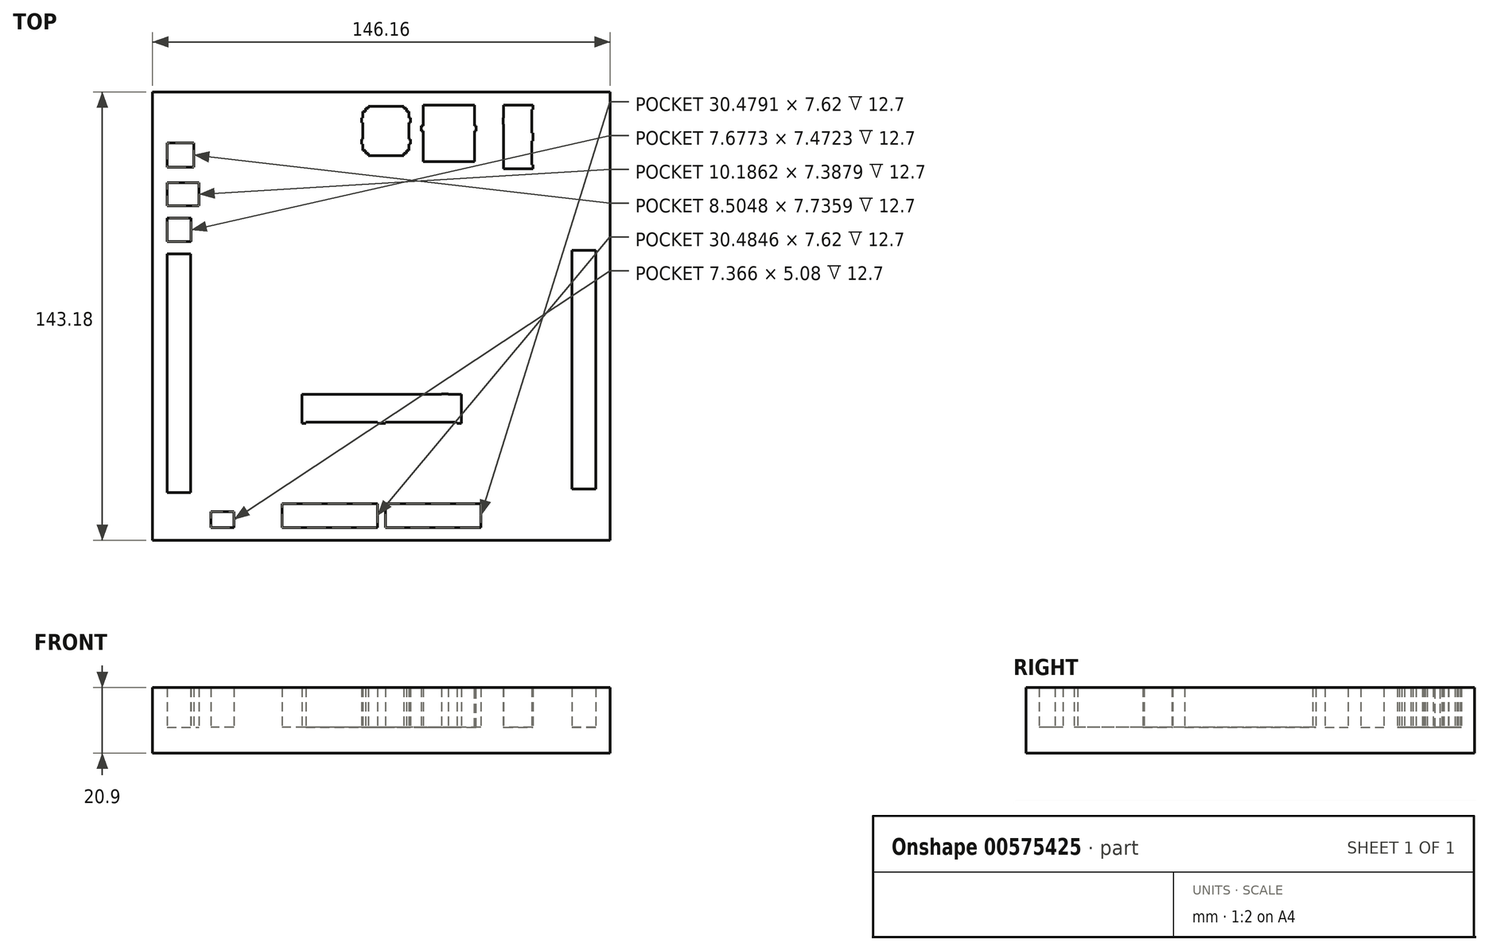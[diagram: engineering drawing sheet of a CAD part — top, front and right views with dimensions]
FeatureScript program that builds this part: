
annotation { "Feature Type Name" : "Feature", "Feature Type Description" : "" }
export const myFeature = defineFeature(function(context is Context, id is Id, definition is map)
    precondition{}
    {
        {
            var Q0;
            Q0=qCreatedBy(makeId("Top.planeOp"),FACE);
            var sketch = newSketch(context, id + "F0", { "sketchPlane" : qUnion([Q0])});
            skLineSegment(sketch, "E0.bottom", {"start": v(73.08, 71.59) * mm, "end": v(-73.08, 71.59) * mm});
            skLineSegment(sketch, "E0.top", {"start": v(73.08, -71.59) * mm, "end": v(-73.08, -71.59) * mm});
            skLineSegment(sketch, "E0.left", {"start": v(73.08, 71.59) * mm, "end": v(73.08, -71.59) * mm});
            skLineSegment(sketch, "E0.right", {"start": v(-73.08, 71.59) * mm, "end": v(-73.08, -71.59) * mm});
            skPoint(sketch, "E0.middle", {"position": v(0, 0) * mm});
            skSolve(sketch);
        }
        {
            var Q0;
            Q0=makeQuery(id+"F0.imprint","IMPRINT",FACE,{"disambiguationData":[TD([[makeQuery(id+"F0.imprint","IMPRINT",EDGE,{"derivedFrom":sQuery(id+"F0.wireOp",EDGE,"E0.bottom")}),1.0]])]});
            extrude(context, id + "F1", {"entities" : qUnion([Q0]), "depth" : 20.9 * mm, "offsetDistance" : 25.4 * mm});
        }
        {
            var Q0;
            Q0=makeQuery(id+"F1.opExtrude","CAP_FACE",FACE,{"disambiguationData":[OSD([sQuery(id+"F0.wireOp",EDGE,"E0.bottom"),sQuery(id+"F0.wireOp",EDGE,"E0.top"),sQuery(id+"F0.wireOp",EDGE,"E0.left"),sQuery(id+"F0.wireOp",EDGE,"E0.right")])],"isStart":false});
            var sketch = newSketch(context, id + "F2", { "sketchPlane" : qUnion([Q0])});
            skLineSegment(sketch, "E1.bottom", {"start": v(68.45, 67.44) * mm, "end": v(-68.45, 67.44) * mm});
            skLineSegment(sketch, "E1.top", {"start": v(68.45, -67.44) * mm, "end": v(-68.45, -67.44) * mm});
            skLineSegment(sketch, "E1.left", {"start": v(68.45, 67.44) * mm, "end": v(68.45, -67.44) * mm});
            skLineSegment(sketch, "E1.right", {"start": v(-68.45, 67.44) * mm, "end": v(-68.45, -67.44) * mm});
            skPoint(sketch, "E1.middle", {"position": v(0, 0) * mm});
            skSolve(sketch);
        }
        {
            var Q0;
            Q0=makeQuery(id+"F2.imprint","IMPRINT",FACE,{"disambiguationData":[TD([[makeQuery(id+"F2.imprint","IMPRINT",EDGE,{"derivedFrom":sQuery(id+"F2.wireOp",EDGE,"E1.bottom")}),1.0]])]});
            extrude(context, id + "F3", {"entities" : qUnion([Q0]), "operationType" : NewBodyOperationType.REMOVE, "oppositeDirection" : true, "depth" : 12.7 * mm, "offsetDistance" : 25.4 * mm});
        }
        {
            var Q0;
            Q0=makeQuery(id+"F3.boolean.opBoolean","COPY",FACE,{"derivedFrom":makeQuery(id+"F3.opExtrude","CAP_FACE",FACE,{"disambiguationData":[OSD([sQuery(id+"F2.wireOp",EDGE,"E1.bottom"),sQuery(id+"F2.wireOp",EDGE,"E1.top"),sQuery(id+"F2.wireOp",EDGE,"E1.left"),sQuery(id+"F2.wireOp",EDGE,"E1.right")])],"isStart":false})});
            var sketch = newSketch(context, id + "F4", { "sketchPlane" : qUnion([Q0])});
            skLineSegment(sketch, "E2.bottom", {"start": v(-68.45, -56.26) * mm, "end": v(-54.48, -56.26) * mm});
            skLineSegment(sketch, "E2.top", {"start": v(-68.45, -67.44) * mm, "end": v(-54.48, -67.44) * mm});
            skLineSegment(sketch, "E2.left", {"start": v(-68.45, -56.26) * mm, "end": v(-68.45, -67.44) * mm});
            skLineSegment(sketch, "E2.right", {"start": v(-54.48, -56.26) * mm, "end": v(-54.48, -67.44) * mm});
            skSolve(sketch);
        }
        {
            var Q0;
            Q0=makeQuery(id+"F4.imprint","IMPRINT",FACE,{"disambiguationData":[TD([[makeQuery(id+"F4.imprint","IMPRINT",EDGE,{"derivedFrom":sQuery(id+"F4.wireOp",EDGE,"E2.bottom")}),-1.0]])]});
            extrude(context, id + "F5", {"entities" : qUnion([Q0]), "operationType" : NewBodyOperationType.ADD, "depth" : 12.7 * mm, "offsetDistance" : 25.4 * mm});
        }
        {
            var Q0;
            Q0=makeQuery(id+"F3.boolean.opBoolean","COPY",FACE,{"derivedFrom":makeQuery(id+"F3.opExtrude","CAP_FACE",FACE,{"disambiguationData":[OSD([sQuery(id+"F2.wireOp",EDGE,"E1.bottom"),sQuery(id+"F2.wireOp",EDGE,"E1.top"),sQuery(id+"F2.wireOp",EDGE,"E1.left"),sQuery(id+"F2.wireOp",EDGE,"E1.right")])],"isStart":false})});
            var sketch = newSketch(context, id + "F6", { "sketchPlane" : qUnion([Q0])});
            skLineSegment(sketch, "E3.bottom", {"start": v(-54.48, -56.26) * mm, "end": v(-31.75, -56.26) * mm});
            skLineSegment(sketch, "E3.top", {"start": v(-54.48, -62.36) * mm, "end": v(-31.75, -62.36) * mm});
            skLineSegment(sketch, "E3.left", {"start": v(-54.48, -56.26) * mm, "end": v(-54.48, -62.36) * mm});
            skLineSegment(sketch, "E3.right", {"start": v(-31.75, -56.26) * mm, "end": v(-31.75, -62.36) * mm});
            skSolve(sketch);
        }
        {
            var Q0;
            Q0=makeQuery(id+"F6.imprint","IMPRINT",FACE,{"disambiguationData":[TD([[makeQuery(id+"F6.imprint","IMPRINT",EDGE,{"derivedFrom":sQuery(id+"F6.wireOp",EDGE,"E3.bottom")}),-1.0]])]});
            extrude(context, id + "F7", {"entities" : qUnion([Q0]), "operationType" : NewBodyOperationType.ADD, "depth" : 12.7 * mm, "offsetDistance" : 25.4 * mm});
        }
        {
            var Q0;
            Q0=makeQuery(id+"F3.boolean.opBoolean","COPY",FACE,{"derivedFrom":makeQuery(id+"F3.opExtrude","CAP_FACE",FACE,{"disambiguationData":[OSD([sQuery(id+"F2.wireOp",EDGE,"E1.bottom"),sQuery(id+"F2.wireOp",EDGE,"E1.top"),sQuery(id+"F2.wireOp",EDGE,"E1.left"),sQuery(id+"F2.wireOp",EDGE,"E1.right")])],"isStart":false})});
            var sketch = newSketch(context, id + "F8", { "sketchPlane" : qUnion([Q0])});
            skLineSegment(sketch, "E4.bottom", {"start": v(-31.75, -62.36) * mm, "end": v(-47.12, -62.36) * mm});
            skLineSegment(sketch, "E4.top", {"start": v(-31.75, -67.44) * mm, "end": v(-47.12, -67.44) * mm});
            skLineSegment(sketch, "E4.left", {"start": v(-31.75, -62.36) * mm, "end": v(-31.75, -67.44) * mm});
            skLineSegment(sketch, "E4.right", {"start": v(-47.12, -62.36) * mm, "end": v(-47.12, -67.44) * mm});
            skSolve(sketch);
        }
        {
            var Q0;
            Q0=makeQuery(id+"F8.imprint","IMPRINT",FACE,{"disambiguationData":[TD([[makeQuery(id+"F8.imprint","IMPRINT",EDGE,{"derivedFrom":sQuery(id+"F8.wireOp",EDGE,"E4.bottom")}),-1.0]])]});
            extrude(context, id + "F9", {"entities" : qUnion([Q0]), "operationType" : NewBodyOperationType.ADD, "depth" : 12.7 * mm, "offsetDistance" : 25.4 * mm});
        }
        {
            var Q0;
            {var subQ0=sQuery(id+"F2.wireOp",EDGE,"E1.right");var subQ1=sQuery(id+"F2.wireOp",EDGE,"E1.left");var subQ2=sQuery(id+"F2.wireOp",EDGE,"E1.top");var subQ3=sQuery(id+"F2.wireOp",EDGE,"E1.bottom");Q0=makeQuery(id+"F9.boolean.opBoolean","SPLIT",FACE,{"disambiguationData":[TD([makeQuery(id+"F3.boolean.opBoolean","COPY",FACE,{"derivedFrom":makeQuery(id+"F3.opExtrude","SWEPT_FACE",FACE,{"disambiguationData":[OSD([subQ3])]})})])],"derivedFrom":makeQuery(id+"F3.boolean.opBoolean","COPY",FACE,{"derivedFrom":makeQuery(id+"F3.opExtrude","CAP_FACE",FACE,{"disambiguationData":[OSD([subQ3,subQ2,subQ1,subQ0])],"isStart":false})})});}
            var sketch = newSketch(context, id + "F10", { "sketchPlane" : qUnion([Q0])});
            skLineSegment(sketch, "E5.bottom", {"start": v(68.45, -55.12) * mm, "end": v(31.75, -55.12) * mm});
            skLineSegment(sketch, "E5.top", {"start": v(68.45, -67.44) * mm, "end": v(31.75, -67.44) * mm});
            skLineSegment(sketch, "E5.left", {"start": v(68.45, -55.12) * mm, "end": v(68.45, -67.44) * mm});
            skLineSegment(sketch, "E5.right", {"start": v(31.75, -55.12) * mm, "end": v(31.75, -67.44) * mm});
            skSolve(sketch);
        }
        {
            var Q0;
            Q0=makeQuery(id+"F10.imprint","IMPRINT",FACE,{"disambiguationData":[TD([[makeQuery(id+"F10.imprint","IMPRINT",EDGE,{"derivedFrom":sQuery(id+"F10.wireOp",EDGE,"E5.bottom")}),1.0]])]});
            extrude(context, id + "F11", {"entities" : qUnion([Q0]), "operationType" : NewBodyOperationType.ADD, "depth" : 12.7 * mm, "offsetDistance" : 25.4 * mm});
        }
        {
            var Q0;
            {var subQ0=sQuery(id+"F2.wireOp",EDGE,"E1.right");var subQ1=sQuery(id+"F2.wireOp",EDGE,"E1.left");var subQ2=sQuery(id+"F2.wireOp",EDGE,"E1.top");var subQ3=sQuery(id+"F2.wireOp",EDGE,"E1.bottom");Q0=makeQuery(id+"F9.boolean.opBoolean","SPLIT",FACE,{"disambiguationData":[TD([makeQuery(id+"F3.boolean.opBoolean","COPY",FACE,{"derivedFrom":makeQuery(id+"F3.opExtrude","SWEPT_FACE",FACE,{"disambiguationData":[OSD([subQ3])]})})])],"derivedFrom":makeQuery(id+"F3.boolean.opBoolean","COPY",FACE,{"derivedFrom":makeQuery(id+"F3.opExtrude","CAP_FACE",FACE,{"disambiguationData":[OSD([subQ3,subQ2,subQ1,subQ0])],"isStart":false})})});}
            var sketch = newSketch(context, id + "F12", { "sketchPlane" : qUnion([Q0])});
            skLineSegment(sketch, "E6.bottom", {"start": v(31.75, -55.12) * mm, "end": v(-60.9, -55.12) * mm});
            skLineSegment(sketch, "E6.top", {"start": v(31.75, -59.82) * mm, "end": v(-60.9, -59.82) * mm});
            skLineSegment(sketch, "E6.left", {"start": v(31.75, -55.12) * mm, "end": v(31.75, -59.82) * mm});
            skLineSegment(sketch, "E6.right", {"start": v(-60.9, -55.12) * mm, "end": v(-60.9, -59.82) * mm});
            skLineSegment(sketch, "E7.left", {"start": v(31.75, -56.26) * mm, "end": v(31.75, -57.82) * mm});
            skSolve(sketch);
        }
        {
            var Q0;
            {var subQ9=sQuery(id+"F12.wireOp",EDGE,"E6.bottom");Q0=makeQuery(id+"F12.imprint","IMPRINT",FACE,{"disambiguationData":[TD([[makeQuery(id+"F12.imprint","IMPRINT",EDGE,{"derivedFrom":subQ9}),1.0]])]});}
            extrude(context, id + "F13", {"entities" : qUnion([Q0]), "operationType" : NewBodyOperationType.ADD, "depth" : 12.7 * mm, "offsetDistance" : 25.4 * mm});
        }
        {
            var Q0;
            {var subQ0=sQuery(id+"F2.wireOp",EDGE,"E1.right");var subQ3=sQuery(id+"F2.wireOp",EDGE,"E1.left");var subQ5=sQuery(id+"F2.wireOp",EDGE,"E1.bottom");var subQ6=makeQuery(id+"F3.boolean.opBoolean","COPY",FACE,{"derivedFrom":makeQuery(id+"F3.opExtrude","SWEPT_FACE",FACE,{"disambiguationData":[OSD([subQ5])]})});var subQ8=sQuery(id+"F2.wireOp",EDGE,"E1.top");Q0=makeQuery(id+"F13.boolean.opBoolean","SPLIT",FACE,{"disambiguationData":[TD([subQ6])],"derivedFrom":makeQuery(id+"F9.boolean.opBoolean","SPLIT",FACE,{"disambiguationData":[TD([subQ6])],"derivedFrom":makeQuery(id+"F3.boolean.opBoolean","COPY",FACE,{"derivedFrom":makeQuery(id+"F3.opExtrude","CAP_FACE",FACE,{"disambiguationData":[OSD([subQ5,subQ8,subQ3,subQ0])],"isStart":false})})})});}
            var sketch = newSketch(context, id + "F14", { "sketchPlane" : qUnion([Q0])});
            skLineSegment(sketch, "E8.bottom", {"start": v(-24.12, -33.89) * mm, "end": v(-1.28, -33.89) * mm});
            skLineSegment(sketch, "E8.top", {"start": v(-24.12, -55.12) * mm, "end": v(-1.28, -55.12) * mm});
            skLineSegment(sketch, "E8.left", {"start": v(-24.12, -33.89) * mm, "end": v(-24.12, -55.12) * mm});
            skLineSegment(sketch, "E8.right", {"start": v(-1.28, -33.89) * mm, "end": v(-1.28, -55.12) * mm});
            skSolve(sketch);
        }
        {
            var Q0;
            Q0=makeQuery(id+"F14.imprint","IMPRINT",FACE,{"disambiguationData":[TD([[makeQuery(id+"F14.imprint","IMPRINT",EDGE,{"derivedFrom":sQuery(id+"F14.wireOp",EDGE,"E8.bottom")}),-1.0]])]});
            extrude(context, id + "F15", {"entities" : qUnion([Q0]), "operationType" : NewBodyOperationType.ADD, "depth" : 12.7 * mm, "offsetDistance" : 25.4 * mm});
        }
        {
            var Q0;
            {var subQ0=sQuery(id+"F2.wireOp",EDGE,"E1.right");var subQ3=sQuery(id+"F2.wireOp",EDGE,"E1.left");var subQ5=sQuery(id+"F2.wireOp",EDGE,"E1.bottom");var subQ6=makeQuery(id+"F3.boolean.opBoolean","COPY",FACE,{"derivedFrom":makeQuery(id+"F3.opExtrude","SWEPT_FACE",FACE,{"disambiguationData":[OSD([subQ5])]})});var subQ8=sQuery(id+"F2.wireOp",EDGE,"E1.top");Q0=makeQuery(id+"F13.boolean.opBoolean","SPLIT",FACE,{"disambiguationData":[TD([subQ6])],"derivedFrom":makeQuery(id+"F9.boolean.opBoolean","SPLIT",FACE,{"disambiguationData":[TD([subQ6])],"derivedFrom":makeQuery(id+"F3.boolean.opBoolean","COPY",FACE,{"derivedFrom":makeQuery(id+"F3.opExtrude","CAP_FACE",FACE,{"disambiguationData":[OSD([subQ5,subQ8,subQ3,subQ0])],"isStart":false})})})});}
            var sketch = newSketch(context, id + "F16", { "sketchPlane" : qUnion([Q0])});
            skLineSegment(sketch, "E9.bottom", {"start": v(-1.28, -55.12) * mm, "end": v(1.76, -55.12) * mm});
            skLineSegment(sketch, "E9.top", {"start": v(-1.28, -34.27) * mm, "end": v(1.76, -34.27) * mm});
            skLineSegment(sketch, "E9.left", {"start": v(-1.28, -55.12) * mm, "end": v(-1.28, -34.27) * mm});
            skLineSegment(sketch, "E9.right", {"start": v(1.76, -55.12) * mm, "end": v(1.76, -34.27) * mm});
            skSolve(sketch);
        }
        {
            var Q0;
            Q0=makeQuery(id+"F16.imprint","IMPRINT",FACE,{"disambiguationData":[TD([[makeQuery(id+"F16.imprint","IMPRINT",EDGE,{"derivedFrom":sQuery(id+"F16.wireOp",EDGE,"E9.bottom")}),-1.0]])]});
            extrude(context, id + "F17", {"entities" : qUnion([Q0]), "operationType" : NewBodyOperationType.ADD, "depth" : 12.7 * mm, "offsetDistance" : 25.4 * mm});
        }
        {
            var Q0;
            {var subQ0=sQuery(id+"F2.wireOp",EDGE,"E1.right");var subQ3=sQuery(id+"F2.wireOp",EDGE,"E1.left");var subQ5=sQuery(id+"F2.wireOp",EDGE,"E1.bottom");var subQ6=makeQuery(id+"F3.boolean.opBoolean","COPY",FACE,{"derivedFrom":makeQuery(id+"F3.opExtrude","SWEPT_FACE",FACE,{"disambiguationData":[OSD([subQ5])]})});var subQ8=sQuery(id+"F2.wireOp",EDGE,"E1.top");Q0=makeQuery(id+"F13.boolean.opBoolean","SPLIT",FACE,{"disambiguationData":[TD([subQ6])],"derivedFrom":makeQuery(id+"F9.boolean.opBoolean","SPLIT",FACE,{"disambiguationData":[TD([subQ6])],"derivedFrom":makeQuery(id+"F3.boolean.opBoolean","COPY",FACE,{"derivedFrom":makeQuery(id+"F3.opExtrude","CAP_FACE",FACE,{"disambiguationData":[OSD([subQ5,subQ8,subQ3,subQ0])],"isStart":false})})})});}
            var sketch = newSketch(context, id + "F18", { "sketchPlane" : qUnion([Q0])});
            skLineSegment(sketch, "E10.bottom", {"start": v(1.26, -33.89) * mm, "end": v(24.12, -33.89) * mm});
            skLineSegment(sketch, "E10.top", {"start": v(1.26, -55.12) * mm, "end": v(24.12, -55.12) * mm});
            skLineSegment(sketch, "E10.left", {"start": v(1.26, -33.89) * mm, "end": v(1.26, -55.12) * mm});
            skLineSegment(sketch, "E10.right", {"start": v(24.12, -33.89) * mm, "end": v(24.12, -55.12) * mm});
            skSolve(sketch);
        }
        {
            var Q0;
            {var subQ1=sQuery(id+"F18.wireOp",EDGE,"E10.bottom");Q0=makeQuery(id+"F18.imprint","IMPRINT",FACE,{"disambiguationData":[TD([[makeQuery(id+"F18.imprint","IMPRINT",EDGE,{"derivedFrom":subQ1}),-1.0]])]});}
            extrude(context, id + "F19", {"entities" : qUnion([Q0]), "operationType" : NewBodyOperationType.ADD, "depth" : 12.7 * mm, "offsetDistance" : 25.4 * mm});
        }
        {
            var Q0;
            {var subQ0=sQuery(id+"F2.wireOp",EDGE,"E1.right");var subQ3=sQuery(id+"F2.wireOp",EDGE,"E1.left");var subQ5=sQuery(id+"F2.wireOp",EDGE,"E1.bottom");var subQ6=makeQuery(id+"F3.boolean.opBoolean","COPY",FACE,{"derivedFrom":makeQuery(id+"F3.opExtrude","SWEPT_FACE",FACE,{"disambiguationData":[OSD([subQ5])]})});var subQ8=sQuery(id+"F2.wireOp",EDGE,"E1.top");Q0=makeQuery(id+"F13.boolean.opBoolean","SPLIT",FACE,{"disambiguationData":[TD([subQ6])],"derivedFrom":makeQuery(id+"F9.boolean.opBoolean","SPLIT",FACE,{"disambiguationData":[TD([subQ6])],"derivedFrom":makeQuery(id+"F3.boolean.opBoolean","COPY",FACE,{"derivedFrom":makeQuery(id+"F3.opExtrude","CAP_FACE",FACE,{"disambiguationData":[OSD([subQ5,subQ8,subQ3,subQ0])],"isStart":false})})})});}
            var sketch = newSketch(context, id + "F20", { "sketchPlane" : qUnion([Q0])});
            skLineSegment(sketch, "E11.bottom", {"start": v(-24.14, -33.89) * mm, "end": v(-24.12, -33.89) * mm});
            skLineSegment(sketch, "E11.top", {"start": v(-24.14, -55.12) * mm, "end": v(-24.12, -55.12) * mm});
            skLineSegment(sketch, "E11.left", {"start": v(-24.14, -33.89) * mm, "end": v(-24.14, -55.12) * mm});
            skLineSegment(sketch, "E11.right", {"start": v(-24.12, -33.89) * mm, "end": v(-24.12, -55.12) * mm});
            skSolve(sketch);
        }
        {
            var Q0;
            Q0=makeQuery(id+"F20.imprint","IMPRINT",FACE,{"disambiguationData":[TD([[makeQuery(id+"F20.imprint","IMPRINT",EDGE,{"derivedFrom":sQuery(id+"F20.wireOp",EDGE,"E11.bottom")}),-1.0]])]});
            extrude(context, id + "F21", {"entities" : qUnion([Q0]), "operationType" : NewBodyOperationType.ADD, "depth" : 12.7 * mm, "offsetDistance" : 25.4 * mm});
        }
        {
            var Q0;
            {var subQ0=sQuery(id+"F2.wireOp",EDGE,"E1.right");var subQ3=sQuery(id+"F2.wireOp",EDGE,"E1.left");var subQ5=sQuery(id+"F2.wireOp",EDGE,"E1.bottom");var subQ6=makeQuery(id+"F3.boolean.opBoolean","COPY",FACE,{"derivedFrom":makeQuery(id+"F3.opExtrude","SWEPT_FACE",FACE,{"disambiguationData":[OSD([subQ5])]})});var subQ8=sQuery(id+"F2.wireOp",EDGE,"E1.top");Q0=makeQuery(id+"F13.boolean.opBoolean","SPLIT",FACE,{"disambiguationData":[TD([subQ6])],"derivedFrom":makeQuery(id+"F9.boolean.opBoolean","SPLIT",FACE,{"disambiguationData":[TD([subQ6])],"derivedFrom":makeQuery(id+"F3.boolean.opBoolean","COPY",FACE,{"derivedFrom":makeQuery(id+"F3.opExtrude","CAP_FACE",FACE,{"disambiguationData":[OSD([subQ5,subQ8,subQ3,subQ0])],"isStart":false})})})});}
            var sketch = newSketch(context, id + "F22", { "sketchPlane" : qUnion([Q0])});
            skLineSegment(sketch, "E12.bottom", {"start": v(24.12, -34.25) * mm, "end": v(60.83, -34.25) * mm});
            skLineSegment(sketch, "E12.top", {"start": v(24.12, -55.12) * mm, "end": v(60.83, -55.12) * mm});
            skLineSegment(sketch, "E12.left", {"start": v(24.12, -34.25) * mm, "end": v(24.12, -55.12) * mm});
            skLineSegment(sketch, "E12.right", {"start": v(60.83, -34.25) * mm, "end": v(60.83, -55.12) * mm});
            skSolve(sketch);
        }
        {
            var Q0;
            Q0=makeQuery(id+"F22.imprint","IMPRINT",FACE,{"disambiguationData":[TD([[makeQuery(id+"F22.imprint","IMPRINT",EDGE,{"derivedFrom":sQuery(id+"F22.wireOp",EDGE,"E12.bottom")}),-1.0]])]});
            extrude(context, id + "F23", {"entities" : qUnion([Q0]), "operationType" : NewBodyOperationType.ADD, "depth" : 12.7 * mm, "offsetDistance" : 25.4 * mm});
        }
        {
            var Q0;
            {var subQ0=sQuery(id+"F2.wireOp",EDGE,"E1.right");var subQ3=sQuery(id+"F2.wireOp",EDGE,"E1.left");var subQ5=sQuery(id+"F2.wireOp",EDGE,"E1.bottom");var subQ6=makeQuery(id+"F3.boolean.opBoolean","COPY",FACE,{"derivedFrom":makeQuery(id+"F3.opExtrude","SWEPT_FACE",FACE,{"disambiguationData":[OSD([subQ5])]})});var subQ8=sQuery(id+"F2.wireOp",EDGE,"E1.top");Q0=makeQuery(id+"F13.boolean.opBoolean","SPLIT",FACE,{"disambiguationData":[TD([subQ6])],"derivedFrom":makeQuery(id+"F9.boolean.opBoolean","SPLIT",FACE,{"disambiguationData":[TD([subQ6])],"derivedFrom":makeQuery(id+"F3.boolean.opBoolean","COPY",FACE,{"derivedFrom":makeQuery(id+"F3.opExtrude","CAP_FACE",FACE,{"disambiguationData":[OSD([subQ5,subQ8,subQ3,subQ0])],"isStart":false})})})});}
            var sketch = newSketch(context, id + "F24", { "sketchPlane" : qUnion([Q0])});
            skLineSegment(sketch, "E13.bottom", {"start": v(60.83, -20.99) * mm, "end": v(25.53, -20.99) * mm});
            skLineSegment(sketch, "E13.top", {"start": v(60.83, -34.25) * mm, "end": v(25.53, -34.25) * mm});
            skLineSegment(sketch, "E13.left", {"start": v(60.83, -20.99) * mm, "end": v(60.83, -34.25) * mm});
            skLineSegment(sketch, "E13.right", {"start": v(25.53, -20.99) * mm, "end": v(25.53, -34.25) * mm});
            skSolve(sketch);
        }
        {
            var Q0;
            Q0=makeQuery(id+"F24.imprint","IMPRINT",FACE,{"disambiguationData":[TD([[makeQuery(id+"F24.imprint","IMPRINT",EDGE,{"derivedFrom":sQuery(id+"F24.wireOp",EDGE,"E13.bottom")}),1.0]])]});
            extrude(context, id + "F25", {"entities" : qUnion([Q0]), "operationType" : NewBodyOperationType.ADD, "depth" : 12.7 * mm, "offsetDistance" : 25.4 * mm});
        }
        {
            var Q0;
            {var subQ0=sQuery(id+"F2.wireOp",EDGE,"E1.right");var subQ3=sQuery(id+"F2.wireOp",EDGE,"E1.left");var subQ5=sQuery(id+"F2.wireOp",EDGE,"E1.bottom");var subQ6=makeQuery(id+"F3.boolean.opBoolean","COPY",FACE,{"derivedFrom":makeQuery(id+"F3.opExtrude","SWEPT_FACE",FACE,{"disambiguationData":[OSD([subQ5])]})});var subQ8=sQuery(id+"F2.wireOp",EDGE,"E1.top");Q0=makeQuery(id+"F13.boolean.opBoolean","SPLIT",FACE,{"disambiguationData":[TD([subQ6])],"derivedFrom":makeQuery(id+"F9.boolean.opBoolean","SPLIT",FACE,{"disambiguationData":[TD([subQ6])],"derivedFrom":makeQuery(id+"F3.boolean.opBoolean","COPY",FACE,{"derivedFrom":makeQuery(id+"F3.opExtrude","CAP_FACE",FACE,{"disambiguationData":[OSD([subQ5,subQ8,subQ3,subQ0])],"isStart":false})})})});}
            var sketch = newSketch(context, id + "F26", { "sketchPlane" : qUnion([Q0])});
            skLineSegment(sketch, "E14.bottom", {"start": v(-60.92, -20.99) * mm, "end": v(-25.62, -20.99) * mm});
            skLineSegment(sketch, "E14.top", {"start": v(-60.92, -55.12) * mm, "end": v(-25.62, -55.12) * mm});
            skLineSegment(sketch, "E14.left", {"start": v(-60.92, -20.99) * mm, "end": v(-60.92, -55.12) * mm});
            skLineSegment(sketch, "E14.right", {"start": v(-25.62, -20.99) * mm, "end": v(-25.62, -55.12) * mm});
            skSolve(sketch);
        }
        {
            var Q0;
            Q0=makeQuery(id+"F26.imprint","IMPRINT",FACE,{"disambiguationData":[TD([[makeQuery(id+"F26.imprint","IMPRINT",EDGE,{"derivedFrom":sQuery(id+"F26.wireOp",EDGE,"E14.bottom")}),-1.0]])]});
            extrude(context, id + "F27", {"entities" : qUnion([Q0]), "operationType" : NewBodyOperationType.ADD, "depth" : 12.7 * mm, "offsetDistance" : 25.4 * mm});
        }
        {
            var Q0;
            {var subQ0=sQuery(id+"F2.wireOp",EDGE,"E1.right");var subQ3=sQuery(id+"F2.wireOp",EDGE,"E1.left");var subQ5=sQuery(id+"F2.wireOp",EDGE,"E1.bottom");var subQ6=makeQuery(id+"F3.boolean.opBoolean","COPY",FACE,{"derivedFrom":makeQuery(id+"F3.opExtrude","SWEPT_FACE",FACE,{"disambiguationData":[OSD([subQ5])]})});var subQ8=sQuery(id+"F2.wireOp",EDGE,"E1.top");Q0=makeQuery(id+"F13.boolean.opBoolean","SPLIT",FACE,{"disambiguationData":[TD([subQ6])],"derivedFrom":makeQuery(id+"F9.boolean.opBoolean","SPLIT",FACE,{"disambiguationData":[TD([subQ6])],"derivedFrom":makeQuery(id+"F3.boolean.opBoolean","COPY",FACE,{"derivedFrom":makeQuery(id+"F3.opExtrude","CAP_FACE",FACE,{"disambiguationData":[OSD([subQ5,subQ8,subQ3,subQ0])],"isStart":false})})})});}
            var sketch = newSketch(context, id + "F28", { "sketchPlane" : qUnion([Q0])});
            skPoint(sketch, "E15.firstSnap0", {"position": v(-0.01, -34.27) * mm});
            skLineSegment(sketch, "E15.bottom", {"start": v(-24.14, -34.27) * mm, "end": v(-25.62, -34.27) * mm});
            skLineSegment(sketch, "E15.top", {"start": v(-24.14, -55.12) * mm, "end": v(-25.62, -55.12) * mm});
            skLineSegment(sketch, "E15.left", {"start": v(-24.14, -34.27) * mm, "end": v(-24.14, -55.12) * mm});
            skLineSegment(sketch, "E15.right", {"start": v(-25.62, -34.27) * mm, "end": v(-25.62, -55.12) * mm});
            skSolve(sketch);
        }
        {
            var Q0;
            Q0=makeQuery(id+"F28.imprint","IMPRINT",FACE,{"disambiguationData":[TD([[makeQuery(id+"F28.imprint","IMPRINT",EDGE,{"derivedFrom":sQuery(id+"F28.wireOp",EDGE,"E15.bottom")}),1.0]])]});
            extrude(context, id + "F29", {"entities" : qUnion([Q0]), "operationType" : NewBodyOperationType.ADD, "depth" : 12.7 * mm, "offsetDistance" : 25.4 * mm});
        }
        {
            var Q0;
            {var subQ0=sQuery(id+"F2.wireOp",EDGE,"E1.right");var subQ3=sQuery(id+"F2.wireOp",EDGE,"E1.left");var subQ5=sQuery(id+"F2.wireOp",EDGE,"E1.bottom");var subQ6=makeQuery(id+"F3.boolean.opBoolean","COPY",FACE,{"derivedFrom":makeQuery(id+"F3.opExtrude","SWEPT_FACE",FACE,{"disambiguationData":[OSD([subQ5])]})});var subQ8=sQuery(id+"F2.wireOp",EDGE,"E1.top");Q0=makeQuery(id+"F13.boolean.opBoolean","SPLIT",FACE,{"disambiguationData":[TD([subQ6])],"derivedFrom":makeQuery(id+"F9.boolean.opBoolean","SPLIT",FACE,{"disambiguationData":[TD([subQ6])],"derivedFrom":makeQuery(id+"F3.boolean.opBoolean","COPY",FACE,{"derivedFrom":makeQuery(id+"F3.opExtrude","CAP_FACE",FACE,{"disambiguationData":[OSD([subQ5,subQ8,subQ3,subQ0])],"isStart":false})})})});}
            var sketch = newSketch(context, id + "F30", { "sketchPlane" : qUnion([Q0])});
            skLineSegment(sketch, "E16.bottom", {"start": v(-25.41, -34.27) * mm, "end": v(-25.62, -34.27) * mm});
            skLineSegment(sketch, "E16.top", {"start": v(-25.41, -20.99) * mm, "end": v(-25.62, -20.99) * mm});
            skLineSegment(sketch, "E16.left", {"start": v(-25.41, -34.27) * mm, "end": v(-25.41, -20.99) * mm});
            skLineSegment(sketch, "E16.right", {"start": v(-25.62, -34.27) * mm, "end": v(-25.62, -20.99) * mm});
            skSolve(sketch);
        }
        {
            var Q0;
            Q0=makeQuery(id+"F30.imprint","IMPRINT",FACE,{"disambiguationData":[TD([[makeQuery(id+"F30.imprint","IMPRINT",EDGE,{"derivedFrom":sQuery(id+"F30.wireOp",EDGE,"E16.bottom")}),-1.0]])]});
            extrude(context, id + "F31", {"entities" : qUnion([Q0]), "operationType" : NewBodyOperationType.ADD, "depth" : 12.7 * mm, "offsetDistance" : 25.4 * mm});
        }
        {
            var Q0;
            {var subQ0=sQuery(id+"F2.wireOp",EDGE,"E1.right");var subQ3=sQuery(id+"F2.wireOp",EDGE,"E1.left");var subQ5=sQuery(id+"F2.wireOp",EDGE,"E1.bottom");var subQ6=makeQuery(id+"F3.boolean.opBoolean","COPY",FACE,{"derivedFrom":makeQuery(id+"F3.opExtrude","SWEPT_FACE",FACE,{"disambiguationData":[OSD([subQ5])]})});var subQ8=sQuery(id+"F2.wireOp",EDGE,"E1.top");Q0=makeQuery(id+"F13.boolean.opBoolean","SPLIT",FACE,{"disambiguationData":[TD([subQ6])],"derivedFrom":makeQuery(id+"F9.boolean.opBoolean","SPLIT",FACE,{"disambiguationData":[TD([subQ6])],"derivedFrom":makeQuery(id+"F3.boolean.opBoolean","COPY",FACE,{"derivedFrom":makeQuery(id+"F3.opExtrude","CAP_FACE",FACE,{"disambiguationData":[OSD([subQ5,subQ8,subQ3,subQ0])],"isStart":false})})})});}
            var sketch = newSketch(context, id + "F32", { "sketchPlane" : qUnion([Q0])});
            skLineSegment(sketch, "E17.bottom", {"start": v(-25.41, -20.99) * mm, "end": v(25.53, -20.99) * mm});
            skLineSegment(sketch, "E17.top", {"start": v(-25.41, -24.8) * mm, "end": v(25.53, -24.8) * mm});
            skLineSegment(sketch, "E17.left", {"start": v(-25.41, -20.99) * mm, "end": v(-25.41, -24.8) * mm});
            skLineSegment(sketch, "E17.right", {"start": v(25.53, -20.99) * mm, "end": v(25.53, -24.8) * mm});
            skSolve(sketch);
        }
        {
            var Q0;
            Q0=makeQuery(id+"F32.imprint","IMPRINT",FACE,{"disambiguationData":[TD([[makeQuery(id+"F32.imprint","IMPRINT",EDGE,{"derivedFrom":sQuery(id+"F32.wireOp",EDGE,"E17.bottom")}),-1.0]])]});
            extrude(context, id + "F33", {"entities" : qUnion([Q0]), "operationType" : NewBodyOperationType.ADD, "depth" : 12.7 * mm, "offsetDistance" : 25.4 * mm});
        }
        {
            var Q0;
            {var subQ0=sQuery(id+"F2.wireOp",EDGE,"E1.right");var subQ3=sQuery(id+"F2.wireOp",EDGE,"E1.left");var subQ5=sQuery(id+"F2.wireOp",EDGE,"E1.bottom");var subQ6=makeQuery(id+"F3.boolean.opBoolean","COPY",FACE,{"derivedFrom":makeQuery(id+"F3.opExtrude","SWEPT_FACE",FACE,{"disambiguationData":[OSD([subQ5])]})});var subQ8=sQuery(id+"F2.wireOp",EDGE,"E1.top");Q0=makeQuery(id+"F33.boolean.opBoolean","SPLIT",FACE,{"disambiguationData":[TD([makeQuery(id+"F15.opExtrude","SWEPT_FACE",FACE,{"disambiguationData":[OSD([sQuery(id+"F14.wireOp",EDGE,"E8.bottom")])]})])],"derivedFrom":makeQuery(id+"F13.boolean.opBoolean","SPLIT",FACE,{"disambiguationData":[TD([subQ6])],"derivedFrom":makeQuery(id+"F9.boolean.opBoolean","SPLIT",FACE,{"disambiguationData":[TD([subQ6])],"derivedFrom":makeQuery(id+"F3.boolean.opBoolean","COPY",FACE,{"derivedFrom":makeQuery(id+"F3.opExtrude","CAP_FACE",FACE,{"disambiguationData":[OSD([subQ5,subQ8,subQ3,subQ0])],"isStart":false})})})})});}
            var sketch = newSketch(context, id + "F34", { "sketchPlane" : qUnion([Q0])});
            skLineSegment(sketch, "E18.bottom", {"start": v(25.53, -24.8) * mm, "end": v(21.33, -24.8) * mm});
            skLineSegment(sketch, "E18.top", {"start": v(25.53, -25) * mm, "end": v(21.33, -25) * mm});
            skLineSegment(sketch, "E18.left", {"start": v(25.53, -24.8) * mm, "end": v(25.53, -25) * mm});
            skLineSegment(sketch, "E18.right", {"start": v(21.33, -24.8) * mm, "end": v(21.33, -25) * mm});
            skLineSegment(sketch, "E19.bottom", {"start": v(25.53, -25) * mm, "end": v(25.39, -25) * mm});
            skLineSegment(sketch, "E19.top", {"start": v(25.53, -34.25) * mm, "end": v(25.39, -34.25) * mm});
            skLineSegment(sketch, "E19.left", {"start": v(25.53, -25) * mm, "end": v(25.53, -34.25) * mm});
            skLineSegment(sketch, "E19.right", {"start": v(25.39, -25) * mm, "end": v(25.39, -34.25) * mm});
            skSolve(sketch);
        }
        {
            var Q0;
            Q0=makeQuery(id+"F34.imprint","IMPRINT",FACE,{"disambiguationData":[TD([[makeQuery(id+"F34.imprint","IMPRINT",EDGE,{"derivedFrom":sQuery(id+"F34.wireOp",EDGE,"E19.bottom")}),1.0]])]});
            var Q1;
            Q1=makeQuery(id+"F34.imprint","IMPRINT",FACE,{"disambiguationData":[TD([[makeQuery(id+"F34.imprint","IMPRINT",EDGE,{"derivedFrom":sQuery(id+"F34.wireOp",EDGE,"E18.bottom")}),-1.0]])]});
            extrude(context, id + "F35", {"entities" : qUnion([Q0, Q1]), "operationType" : NewBodyOperationType.ADD, "depth" : 12.7 * mm, "offsetDistance" : 25.4 * mm});
        }
        {
            var Q0;
            {var subQ0=sQuery(id+"F2.wireOp",EDGE,"E1.right");var subQ3=sQuery(id+"F2.wireOp",EDGE,"E1.left");var subQ5=sQuery(id+"F2.wireOp",EDGE,"E1.bottom");var subQ6=makeQuery(id+"F3.boolean.opBoolean","COPY",FACE,{"derivedFrom":makeQuery(id+"F3.opExtrude","SWEPT_FACE",FACE,{"disambiguationData":[OSD([subQ5])]})});var subQ8=sQuery(id+"F2.wireOp",EDGE,"E1.top");Q0=makeQuery(id+"F33.boolean.opBoolean","SPLIT",FACE,{"disambiguationData":[TD([makeQuery(id+"F15.opExtrude","SWEPT_FACE",FACE,{"disambiguationData":[OSD([sQuery(id+"F14.wireOp",EDGE,"E8.bottom")])]})])],"derivedFrom":makeQuery(id+"F13.boolean.opBoolean","SPLIT",FACE,{"disambiguationData":[TD([subQ6])],"derivedFrom":makeQuery(id+"F9.boolean.opBoolean","SPLIT",FACE,{"disambiguationData":[TD([subQ6])],"derivedFrom":makeQuery(id+"F3.boolean.opBoolean","COPY",FACE,{"derivedFrom":makeQuery(id+"F3.opExtrude","CAP_FACE",FACE,{"disambiguationData":[OSD([subQ5,subQ8,subQ3,subQ0])],"isStart":false})})})})});}
            var sketch = newSketch(context, id + "F36", { "sketchPlane" : qUnion([Q0])});
            skLineSegment(sketch, "E20.bottom", {"start": v(19.3, -25) * mm, "end": v(-25.41, -25) * mm});
            skLineSegment(sketch, "E20.top", {"start": v(19.3, -24.8) * mm, "end": v(-25.41, -24.8) * mm});
            skLineSegment(sketch, "E20.left", {"start": v(19.3, -25) * mm, "end": v(19.3, -24.8) * mm});
            skLineSegment(sketch, "E20.right", {"start": v(-25.41, -25) * mm, "end": v(-25.41, -24.8) * mm});
            skSolve(sketch);
        }
        {
            var Q0;
            Q0=makeQuery(id+"F36.imprint","IMPRINT",FACE,{"disambiguationData":[TD([[makeQuery(id+"F36.imprint","IMPRINT",EDGE,{"derivedFrom":sQuery(id+"F36.wireOp",EDGE,"E20.bottom")}),-1.0]])]});
            extrude(context, id + "F37", {"entities" : qUnion([Q0]), "operationType" : NewBodyOperationType.ADD, "depth" : 12.7 * mm, "offsetDistance" : 25.4 * mm});
        }
        {
            var Q0;
            {var subQ3=sQuery(id+"F2.wireOp",EDGE,"E1.bottom");var subQ4=makeQuery(id+"F3.boolean.opBoolean","COPY",FACE,{"derivedFrom":makeQuery(id+"F3.opExtrude","SWEPT_FACE",FACE,{"disambiguationData":[OSD([subQ3])]})});var subQ5=sQuery(id+"F2.wireOp",EDGE,"E1.left");var subQ8=sQuery(id+"F2.wireOp",EDGE,"E1.right");var subQ11=sQuery(id+"F2.wireOp",EDGE,"E1.top");Q0=makeQuery(id+"F33.boolean.opBoolean","SPLIT",FACE,{"disambiguationData":[TD([subQ4])],"derivedFrom":makeQuery(id+"F13.boolean.opBoolean","SPLIT",FACE,{"disambiguationData":[TD([subQ4])],"derivedFrom":makeQuery(id+"F9.boolean.opBoolean","SPLIT",FACE,{"disambiguationData":[TD([subQ4])],"derivedFrom":makeQuery(id+"F3.boolean.opBoolean","COPY",FACE,{"derivedFrom":makeQuery(id+"F3.opExtrude","CAP_FACE",FACE,{"disambiguationData":[OSD([subQ3,subQ11,subQ5,subQ8])],"isStart":false})})})})});}
            var sketch = newSketch(context, id + "F38", { "sketchPlane" : qUnion([Q0])});
            skLineSegment(sketch, "E21.bottom", {"start": v(-68.45, 23.82) * mm, "end": v(-59.52, 23.82) * mm});
            skLineSegment(sketch, "E21.top", {"start": v(-68.45, 19.9) * mm, "end": v(-59.52, 19.9) * mm});
            skLineSegment(sketch, "E21.left", {"start": v(-68.45, 23.82) * mm, "end": v(-68.45, 19.9) * mm});
            skLineSegment(sketch, "E21.right", {"start": v(-59.52, 23.82) * mm, "end": v(-59.52, 19.9) * mm});
            skSolve(sketch);
        }
        {
            var Q0;
            Q0=makeQuery(id+"F38.imprint","IMPRINT",FACE,{"disambiguationData":[TD([[makeQuery(id+"F38.imprint","IMPRINT",EDGE,{"derivedFrom":sQuery(id+"F38.wireOp",EDGE,"E21.bottom")}),-1.0]])]});
            extrude(context, id + "F39", {"entities" : qUnion([Q0]), "operationType" : NewBodyOperationType.ADD, "depth" : 12.7 * mm, "offsetDistance" : 25.4 * mm});
        }
        {
            var Q0;
            {var subQ3=sQuery(id+"F2.wireOp",EDGE,"E1.bottom");var subQ4=makeQuery(id+"F3.boolean.opBoolean","COPY",FACE,{"derivedFrom":makeQuery(id+"F3.opExtrude","SWEPT_FACE",FACE,{"disambiguationData":[OSD([subQ3])]})});var subQ5=sQuery(id+"F2.wireOp",EDGE,"E1.left");var subQ8=sQuery(id+"F2.wireOp",EDGE,"E1.right");var subQ11=sQuery(id+"F2.wireOp",EDGE,"E1.top");Q0=makeQuery(id+"F33.boolean.opBoolean","SPLIT",FACE,{"disambiguationData":[TD([subQ4])],"derivedFrom":makeQuery(id+"F13.boolean.opBoolean","SPLIT",FACE,{"disambiguationData":[TD([subQ4])],"derivedFrom":makeQuery(id+"F9.boolean.opBoolean","SPLIT",FACE,{"disambiguationData":[TD([subQ4])],"derivedFrom":makeQuery(id+"F3.boolean.opBoolean","COPY",FACE,{"derivedFrom":makeQuery(id+"F3.opExtrude","CAP_FACE",FACE,{"disambiguationData":[OSD([subQ3,subQ11,subQ5,subQ8])],"isStart":false})})})})});}
            var sketch = newSketch(context, id + "F40", { "sketchPlane" : qUnion([Q0])});
            skLineSegment(sketch, "E22.bottom", {"start": v(-59.52, 23.82) * mm, "end": v(68.45, 23.82) * mm});
            skLineSegment(sketch, "E22.top", {"start": v(-59.52, 21.01) * mm, "end": v(68.45, 21.01) * mm});
            skLineSegment(sketch, "E22.left", {"start": v(-59.52, 23.82) * mm, "end": v(-59.52, 21.01) * mm});
            skLineSegment(sketch, "E22.right", {"start": v(68.45, 23.82) * mm, "end": v(68.45, 21.01) * mm});
            skSolve(sketch);
        }
        {
            var Q0;
            Q0=makeQuery(id+"F40.imprint","IMPRINT",FACE,{"disambiguationData":[TD([[makeQuery(id+"F40.imprint","IMPRINT",EDGE,{"derivedFrom":sQuery(id+"F40.wireOp",EDGE,"E22.bottom")}),-1.0]])]});
            extrude(context, id + "F41", {"entities" : qUnion([Q0]), "operationType" : NewBodyOperationType.ADD, "depth" : 12.7 * mm, "offsetDistance" : 25.4 * mm});
        }
        {
            var Q0;
            {var subQ5=sQuery(id+"F2.wireOp",EDGE,"E1.left");var subQ7=makeQuery(id+"F5.opExtrude","SWEPT_FACE",FACE,{"disambiguationData":[OSD([sQuery(id+"F4.wireOp",EDGE,"E2.bottom")])]});var subQ8=sQuery(id+"F2.wireOp",EDGE,"E1.right");var subQ17=sQuery(id+"F2.wireOp",EDGE,"E1.bottom");var subQ18=makeQuery(id+"F3.boolean.opBoolean","COPY",FACE,{"derivedFrom":makeQuery(id+"F3.opExtrude","SWEPT_FACE",FACE,{"disambiguationData":[OSD([subQ17])]})});var subQ19=sQuery(id+"F2.wireOp",EDGE,"E1.top");Q0=makeQuery(id+"F41.boolean.opBoolean","SPLIT",FACE,{"disambiguationData":[TD([subQ7])],"derivedFrom":makeQuery(id+"F33.boolean.opBoolean","SPLIT",FACE,{"disambiguationData":[TD([subQ18])],"derivedFrom":makeQuery(id+"F13.boolean.opBoolean","SPLIT",FACE,{"disambiguationData":[TD([subQ18])],"derivedFrom":makeQuery(id+"F9.boolean.opBoolean","SPLIT",FACE,{"disambiguationData":[TD([subQ18])],"derivedFrom":makeQuery(id+"F3.boolean.opBoolean","COPY",FACE,{"derivedFrom":makeQuery(id+"F3.opExtrude","CAP_FACE",FACE,{"disambiguationData":[OSD([subQ17,subQ19,subQ5,subQ8])],"isStart":false})})})})})});}
            var sketch = newSketch(context, id + "F42", { "sketchPlane" : qUnion([Q0])});
            skLineSegment(sketch, "E23.bottom", {"start": v(-59.52, 19.9) * mm, "end": v(60.87, 19.9) * mm});
            skLineSegment(sketch, "E23.top", {"start": v(-59.52, 21.01) * mm, "end": v(60.87, 21.01) * mm});
            skLineSegment(sketch, "E23.left", {"start": v(-59.52, 19.9) * mm, "end": v(-59.52, 21.01) * mm});
            skLineSegment(sketch, "E23.right", {"start": v(60.87, 19.9) * mm, "end": v(60.87, 21.01) * mm});
            skSolve(sketch);
        }
        {
            var Q0;
            Q0=makeQuery(id+"F42.imprint","IMPRINT",FACE,{"disambiguationData":[TD([[makeQuery(id+"F42.imprint","IMPRINT",EDGE,{"derivedFrom":sQuery(id+"F42.wireOp",EDGE,"E23.bottom")}),1.0]])]});
            extrude(context, id + "F43", {"entities" : qUnion([Q0]), "operationType" : NewBodyOperationType.ADD, "depth" : 12.7 * mm, "offsetDistance" : 25.4 * mm});
        }
        {
            var Q0;
            {var subQ5=sQuery(id+"F2.wireOp",EDGE,"E1.left");var subQ7=makeQuery(id+"F5.opExtrude","SWEPT_FACE",FACE,{"disambiguationData":[OSD([sQuery(id+"F4.wireOp",EDGE,"E2.bottom")])]});var subQ8=sQuery(id+"F2.wireOp",EDGE,"E1.right");var subQ17=sQuery(id+"F2.wireOp",EDGE,"E1.bottom");var subQ18=makeQuery(id+"F3.boolean.opBoolean","COPY",FACE,{"derivedFrom":makeQuery(id+"F3.opExtrude","SWEPT_FACE",FACE,{"disambiguationData":[OSD([subQ17])]})});var subQ19=sQuery(id+"F2.wireOp",EDGE,"E1.top");Q0=makeQuery(id+"F41.boolean.opBoolean","SPLIT",FACE,{"disambiguationData":[TD([subQ7])],"derivedFrom":makeQuery(id+"F33.boolean.opBoolean","SPLIT",FACE,{"disambiguationData":[TD([subQ18])],"derivedFrom":makeQuery(id+"F13.boolean.opBoolean","SPLIT",FACE,{"disambiguationData":[TD([subQ18])],"derivedFrom":makeQuery(id+"F9.boolean.opBoolean","SPLIT",FACE,{"disambiguationData":[TD([subQ18])],"derivedFrom":makeQuery(id+"F3.boolean.opBoolean","COPY",FACE,{"derivedFrom":makeQuery(id+"F3.opExtrude","CAP_FACE",FACE,{"disambiguationData":[OSD([subQ17,subQ19,subQ5,subQ8])],"isStart":false})})})})})});}
            var sketch = newSketch(context, id + "F44", { "sketchPlane" : qUnion([Q0])});
            skLineSegment(sketch, "E24.bottom", {"start": v(-60.92, -20.99) * mm, "end": v(60.87, -20.99) * mm});
            skLineSegment(sketch, "E24.top", {"start": v(-60.92, 19.9) * mm, "end": v(60.87, 19.9) * mm});
            skLineSegment(sketch, "E24.left", {"start": v(-60.92, -20.99) * mm, "end": v(-60.92, 19.9) * mm});
            skLineSegment(sketch, "E24.right", {"start": v(60.87, -20.99) * mm, "end": v(60.87, 19.9) * mm});
            skSolve(sketch);
        }
        {
            var Q0;
            Q0=makeQuery(id+"F44.imprint","IMPRINT",FACE,{"disambiguationData":[TD([[makeQuery(id+"F44.imprint","IMPRINT",EDGE,{"derivedFrom":sQuery(id+"F44.wireOp",EDGE,"E24.top")}),-1.0]])]});
            extrude(context, id + "F45", {"entities" : qUnion([Q0]), "operationType" : NewBodyOperationType.ADD, "depth" : 12.7 * mm, "offsetDistance" : 25.4 * mm});
        }
        {
            var Q0;
            {var subQ0=sQuery(id+"F2.wireOp",EDGE,"E1.right");var subQ2=sQuery(id+"F2.wireOp",EDGE,"E1.left");var subQ4=sQuery(id+"F2.wireOp",EDGE,"E1.bottom");var subQ5=makeQuery(id+"F3.boolean.opBoolean","COPY",FACE,{"derivedFrom":makeQuery(id+"F3.opExtrude","SWEPT_FACE",FACE,{"disambiguationData":[OSD([subQ4])]})});var subQ11=sQuery(id+"F2.wireOp",EDGE,"E1.top");Q0=makeQuery(id+"F41.boolean.opBoolean","SPLIT",FACE,{"disambiguationData":[TD([subQ5])],"derivedFrom":makeQuery(id+"F33.boolean.opBoolean","SPLIT",FACE,{"disambiguationData":[TD([subQ5])],"derivedFrom":makeQuery(id+"F13.boolean.opBoolean","SPLIT",FACE,{"disambiguationData":[TD([subQ5])],"derivedFrom":makeQuery(id+"F9.boolean.opBoolean","SPLIT",FACE,{"disambiguationData":[TD([subQ5])],"derivedFrom":makeQuery(id+"F3.boolean.opBoolean","COPY",FACE,{"derivedFrom":makeQuery(id+"F3.opExtrude","CAP_FACE",FACE,{"disambiguationData":[OSD([subQ4,subQ11,subQ2,subQ0])],"isStart":false})})})})})});}
            var sketch = newSketch(context, id + "F46", { "sketchPlane" : qUnion([Q0])});
            skLineSegment(sketch, "E25.bottom", {"start": v(-68.45, 35.25) * mm, "end": v(-56.12, 35.25) * mm});
            skLineSegment(sketch, "E25.top", {"start": v(-68.45, 31.29) * mm, "end": v(-56.12, 31.29) * mm});
            skLineSegment(sketch, "E25.left", {"start": v(-68.45, 35.25) * mm, "end": v(-68.45, 31.29) * mm});
            skLineSegment(sketch, "E25.right", {"start": v(-56.12, 35.25) * mm, "end": v(-56.12, 31.29) * mm});
            skSolve(sketch);
        }
        {
            var Q0;
            Q0=makeQuery(id+"F46.imprint","IMPRINT",FACE,{"disambiguationData":[TD([[makeQuery(id+"F46.imprint","IMPRINT",EDGE,{"derivedFrom":sQuery(id+"F46.wireOp",EDGE,"E25.bottom")}),-1.0]])]});
            extrude(context, id + "F47", {"entities" : qUnion([Q0]), "operationType" : NewBodyOperationType.ADD, "depth" : 12.7 * mm, "offsetDistance" : 25.4 * mm});
        }
        {
            var Q0;
            {var subQ0=sQuery(id+"F2.wireOp",EDGE,"E1.right");var subQ2=sQuery(id+"F2.wireOp",EDGE,"E1.left");var subQ4=sQuery(id+"F2.wireOp",EDGE,"E1.bottom");var subQ5=makeQuery(id+"F3.boolean.opBoolean","COPY",FACE,{"derivedFrom":makeQuery(id+"F3.opExtrude","SWEPT_FACE",FACE,{"disambiguationData":[OSD([subQ4])]})});var subQ11=sQuery(id+"F2.wireOp",EDGE,"E1.top");Q0=makeQuery(id+"F41.boolean.opBoolean","SPLIT",FACE,{"disambiguationData":[TD([subQ5])],"derivedFrom":makeQuery(id+"F33.boolean.opBoolean","SPLIT",FACE,{"disambiguationData":[TD([subQ5])],"derivedFrom":makeQuery(id+"F13.boolean.opBoolean","SPLIT",FACE,{"disambiguationData":[TD([subQ5])],"derivedFrom":makeQuery(id+"F9.boolean.opBoolean","SPLIT",FACE,{"disambiguationData":[TD([subQ5])],"derivedFrom":makeQuery(id+"F3.boolean.opBoolean","COPY",FACE,{"derivedFrom":makeQuery(id+"F3.opExtrude","CAP_FACE",FACE,{"disambiguationData":[OSD([subQ4,subQ11,subQ2,subQ0])],"isStart":false})})})})})});}
            var sketch = newSketch(context, id + "F48", { "sketchPlane" : qUnion([Q0])});
            skLineSegment(sketch, "E26", {"start": v(-58.27, 35.25) * mm, "end": v(-58.27, 42.64) * mm});
            skLineSegment(sketch, "E27", {"start": v(-58.27, 42.64) * mm, "end": v(-68.45, 42.64) * mm});
            skLineSegment(sketch, "E28", {"start": v(-68.45, 42.64) * mm, "end": v(-68.45, 47.59) * mm});
            skLineSegment(sketch, "E29", {"start": v(-68.45, 47.59) * mm, "end": v(-56.12, 47.59) * mm});
            skLineSegment(sketch, "E30", {"start": v(-56.12, 47.59) * mm, "end": v(-56.12, 35.25) * mm});
            skLineSegment(sketch, "E31", {"start": v(-56.12, 35.25) * mm, "end": v(-58.27, 35.25) * mm});
            skLineSegment(sketch, "E32", {"start": v(-56.12, 31.29) * mm, "end": v(-56.12, 23.82) * mm});
            skLineSegment(sketch, "E33", {"start": v(-56.12, 23.82) * mm, "end": v(-60.78, 23.82) * mm});
            skLineSegment(sketch, "E34", {"start": v(-60.78, 23.82) * mm, "end": v(-60.78, 31.29) * mm});
            skLineSegment(sketch, "E35", {"start": v(-60.78, 31.29) * mm, "end": v(-56.12, 31.29) * mm});
            skLineSegment(sketch, "E36", {"start": v(-59.95, 47.59) * mm, "end": v(-59.95, 55.32) * mm});
            skLineSegment(sketch, "E37", {"start": v(-59.95, 55.32) * mm, "end": v(-68.45, 55.32) * mm});
            skLineSegment(sketch, "E38", {"start": v(-68.45, 55.32) * mm, "end": v(-68.45, 67.44) * mm});
            skLineSegment(sketch, "E39", {"start": v(-68.45, 67.44) * mm, "end": v(-7.62, 67.44) * mm});
            skLineSegment(sketch, "E40", {"start": v(-7.62, 67.44) * mm, "end": v(-7.62, 47.59) * mm});
            skLineSegment(sketch, "E41", {"start": v(-7.62, 47.59) * mm, "end": v(-59.95, 47.59) * mm});
            skSolve(sketch);
        }
        {
            var Q0;
            {var subQ0=sQuery(id+"F48.wireOp",EDGE,"E36");Q0=makeQuery(id+"F48.imprint","IMPRINT",FACE,{"disambiguationData":[TD([[makeQuery(id+"F48.imprint","IMPRINT",EDGE,{"derivedFrom":subQ0}),-1.0]])]});}
            var Q1;
            Q1=makeQuery(id+"F48.imprint","IMPRINT",FACE,{"disambiguationData":[TD([[makeQuery(id+"F48.imprint","IMPRINT",EDGE,{"derivedFrom":sQuery(id+"F48.wireOp",EDGE,"E26")}),-1.0]])]});
            var Q2;
            Q2=makeQuery(id+"F48.imprint","IMPRINT",FACE,{"disambiguationData":[TD([[makeQuery(id+"F48.imprint","IMPRINT",EDGE,{"derivedFrom":sQuery(id+"F48.wireOp",EDGE,"E32")}),-1.0]])]});
            extrude(context, id + "F49", {"entities" : qUnion([Q0, Q1, Q2]), "operationType" : NewBodyOperationType.ADD, "depth" : 12.7 * mm, "offsetDistance" : 25.4 * mm});
        }
        {
            var Q0;
            {var subQ1=sQuery(id+"F2.wireOp",EDGE,"E1.left");var subQ4=sQuery(id+"F2.wireOp",EDGE,"E1.bottom");var subQ5=makeQuery(id+"F3.boolean.opBoolean","COPY",FACE,{"derivedFrom":makeQuery(id+"F3.opExtrude","SWEPT_FACE",FACE,{"disambiguationData":[OSD([subQ4])]})});var subQ6=sQuery(id+"F2.wireOp",EDGE,"E1.right");var subQ13=sQuery(id+"F2.wireOp",EDGE,"E1.top");Q0=makeQuery(id+"F49.boolean.opBoolean","SPLIT",FACE,{"disambiguationData":[TD([subQ5])],"derivedFrom":makeQuery(id+"F41.boolean.opBoolean","SPLIT",FACE,{"disambiguationData":[TD([subQ5])],"derivedFrom":makeQuery(id+"F33.boolean.opBoolean","SPLIT",FACE,{"disambiguationData":[TD([subQ5])],"derivedFrom":makeQuery(id+"F13.boolean.opBoolean","SPLIT",FACE,{"disambiguationData":[TD([subQ5])],"derivedFrom":makeQuery(id+"F9.boolean.opBoolean","SPLIT",FACE,{"disambiguationData":[TD([subQ5])],"derivedFrom":makeQuery(id+"F3.boolean.opBoolean","COPY",FACE,{"derivedFrom":makeQuery(id+"F3.opExtrude","CAP_FACE",FACE,{"disambiguationData":[OSD([subQ4,subQ13,subQ1,subQ6])],"isStart":false})})})})})})});}
            var sketch = newSketch(context, id + "F50", { "sketchPlane" : qUnion([Q0])});
            skLineSegment(sketch, "E42", {"start": v(13.39, 66.39) * mm, "end": v(13.39, 60.72) * mm});
            skLineSegment(sketch, "E43", {"start": v(13.39, 60.72) * mm, "end": v(12.8, 60.72) * mm});
            skLineSegment(sketch, "E44", {"start": v(12.8, 60.72) * mm, "end": v(12.8, 59.1) * mm});
            skLineSegment(sketch, "E45", {"start": v(12.8, 59.1) * mm, "end": v(13.39, 59.1) * mm});
            skLineSegment(sketch, "E46", {"start": v(13.39, 59.1) * mm, "end": v(13.39, 49.33) * mm});
            skLineSegment(sketch, "E47", {"start": v(13.39, 49.33) * mm, "end": v(29.74, 49.33) * mm});
            skLineSegment(sketch, "E48", {"start": v(29.74, 49.33) * mm, "end": v(29.74, 67.44) * mm});
            skLineSegment(sketch, "E49", {"start": v(29.74, 67.44) * mm, "end": v(36.72, 67.44) * mm});
            skLineSegment(sketch, "E50", {"start": v(36.72, 67.44) * mm, "end": v(36.72, 47.59) * mm});
            skLineSegment(sketch, "E51", {"start": v(36.72, 47.59) * mm, "end": v(11, 47.59) * mm});
            skLineSegment(sketch, "E52", {"start": v(11, 47.59) * mm, "end": v(11, 67.44) * mm});
            skLineSegment(sketch, "E53", {"start": v(11, 67.44) * mm, "end": v(13.39, 67.44) * mm});
            skLineSegment(sketch, "E54", {"start": v(13.39, 67.44) * mm, "end": v(13.39, 66.39) * mm});
            skLineSegment(sketch, "E55.bottom", {"start": v(13.39, 67.44) * mm, "end": v(29.74, 67.44) * mm});
            skLineSegment(sketch, "E55.top", {"start": v(13.39, 66.33) * mm, "end": v(29.74, 66.33) * mm});
            skLineSegment(sketch, "E55.left", {"start": v(13.39, 67.44) * mm, "end": v(13.39, 66.33) * mm});
            skLineSegment(sketch, "E55.right", {"start": v(29.74, 67.44) * mm, "end": v(29.74, 66.33) * mm});
            skSolve(sketch);
        }
        {
            var Q0;
            Q0=makeQuery(id+"F50.imprint","IMPRINT",FACE,{"disambiguationData":[TD([[makeQuery(id+"F50.imprint","IMPRINT",EDGE,{"derivedFrom":sQuery(id+"F50.wireOp",EDGE,"E42")}),-1.0]])]});
            extrude(context, id + "F51", {"entities" : qUnion([Q0]), "operationType" : NewBodyOperationType.ADD, "depth" : 12.7 * mm, "offsetDistance" : 25.4 * mm});
        }
        {
            var Q0;
            {var subQ0=sQuery(id+"F16.wireOp",EDGE,"E9.right");var subQ1=sQuery(id+"F16.wireOp",EDGE,"E9.top");var subQ2=sQuery(id+"F8.wireOp",EDGE,"E4.left");var subQ3=sQuery(id+"F6.wireOp",EDGE,"E3.right");var subQ4=sQuery(id+"F6.wireOp",EDGE,"E3.bottom");var subQ5=sQuery(id+"F4.wireOp",EDGE,"E2.bottom");Q0=makeQuery(id+"F51.boolean.opBoolean","MERGE",FACE,{"derivedFrom":[makeQuery(id+"F49.boolean.opBoolean","MERGE",FACE,{"derivedFrom":[makeQuery(id+"F47.boolean.opBoolean","MERGE",FACE,{"derivedFrom":[makeQuery(id+"F45.boolean.opBoolean","MERGE",FACE,{"derivedFrom":[makeQuery(id+"F43.boolean.opBoolean","MERGE",FACE,{"derivedFrom":[makeQuery(id+"F41.boolean.opBoolean","MERGE",FACE,{"derivedFrom":[makeQuery(id+"F39.boolean.opBoolean","MERGE",FACE,{"derivedFrom":[makeQuery(id+"F37.boolean.opBoolean","MERGE",FACE,{"derivedFrom":[makeQuery(id+"F35.boolean.opBoolean","MERGE",FACE,{"derivedFrom":[makeQuery(id+"F33.boolean.opBoolean","MERGE",FACE,{"derivedFrom":[makeQuery(id+"F31.boolean.opBoolean","MERGE",FACE,{"derivedFrom":[makeQuery(id+"F29.boolean.opBoolean","MERGE",FACE,{"derivedFrom":[makeQuery(id+"F27.boolean.opBoolean","MERGE",FACE,{"derivedFrom":[makeQuery(id+"F25.boolean.opBoolean","MERGE",FACE,{"derivedFrom":[makeQuery(id+"F23.boolean.opBoolean","MERGE",FACE,{"derivedFrom":[makeQuery(id+"F21.boolean.opBoolean","MERGE",FACE,{"derivedFrom":[makeQuery(id+"F19.boolean.opBoolean","MERGE",FACE,{"derivedFrom":[makeQuery(id+"F17.boolean.opBoolean","MERGE",FACE,{"derivedFrom":[makeQuery(id+"F15.boolean.opBoolean","MERGE",FACE,{"derivedFrom":[makeQuery(id+"F13.boolean.opBoolean","MERGE",FACE,{"derivedFrom":[makeQuery(id+"F11.boolean.opBoolean","MERGE",FACE,{"derivedFrom":[makeQuery(id+"F9.boolean.opBoolean","MERGE",FACE,{"derivedFrom":[makeQuery(id+"F7.boolean.opBoolean","MERGE",FACE,{"derivedFrom":[makeQuery(id+"F5.boolean.opBoolean","MERGE",FACE,{"derivedFrom":[makeQuery(id+"F1.opExtrude","CAP_FACE",FACE,{"disambiguationData":[OSD([sQuery(id+"F0.wireOp",EDGE,"E0.bottom"),sQuery(id+"F0.wireOp",EDGE,"E0.top"),sQuery(id+"F0.wireOp",EDGE,"E0.left"),sQuery(id+"F0.wireOp",EDGE,"E0.right")])],"isStart":false}),makeQuery(id+"F5.opExtrude","CAP_FACE",FACE,{"disambiguationData":[OSD([subQ5,sQuery(id+"F4.wireOp",EDGE,"E2.top"),sQuery(id+"F4.wireOp",EDGE,"E2.left"),sQuery(id+"F4.wireOp",EDGE,"E2.right")])],"isStart":false})]}),makeQuery(id+"F7.opExtrude","CAP_FACE",FACE,{"disambiguationData":[OSD([subQ4,sQuery(id+"F6.wireOp",EDGE,"E3.top"),sQuery(id+"F6.wireOp",EDGE,"E3.left"),subQ3])],"isStart":false})]}),makeQuery(id+"F9.opExtrude","CAP_FACE",FACE,{"disambiguationData":[OSD([sQuery(id+"F8.wireOp",EDGE,"E4.bottom"),sQuery(id+"F8.wireOp",EDGE,"E4.top"),subQ2,sQuery(id+"F8.wireOp",EDGE,"E4.right")])],"isStart":false})]}),makeQuery(id+"F11.opExtrude","CAP_FACE",FACE,{"disambiguationData":[OSD([sQuery(id+"F10.wireOp",EDGE,"E5.bottom"),sQuery(id+"F10.wireOp",EDGE,"E5.top"),sQuery(id+"F10.wireOp",EDGE,"E5.left"),sQuery(id+"F10.wireOp",EDGE,"E5.right")])],"isStart":false})]}),makeQuery(id+"F13.opExtrude","CAP_FACE",FACE,{"disambiguationData":[OSD([subQ5,subQ4,subQ3,subQ2,sQuery(id+"F12.wireOp",EDGE,"E6.bottom"),sQuery(id+"F12.wireOp",EDGE,"E6.top"),sQuery(id+"F12.wireOp",EDGE,"E6.left"),sQuery(id+"F12.wireOp",EDGE,"E6.right"),sQuery(id+"F12.wireOp",EDGE,"E7.left")])],"isStart":false})]}),makeQuery(id+"F15.opExtrude","CAP_FACE",FACE,{"disambiguationData":[OSD([sQuery(id+"F14.wireOp",EDGE,"E8.bottom"),sQuery(id+"F14.wireOp",EDGE,"E8.top"),sQuery(id+"F14.wireOp",EDGE,"E8.left"),sQuery(id+"F14.wireOp",EDGE,"E8.right")])],"isStart":false})]}),makeQuery(id+"F17.opExtrude","CAP_FACE",FACE,{"disambiguationData":[OSD([sQuery(id+"F16.wireOp",EDGE,"E9.bottom"),subQ1,sQuery(id+"F16.wireOp",EDGE,"E9.left"),subQ0])],"isStart":false})]}),makeQuery(id+"F19.opExtrude","CAP_FACE",FACE,{"disambiguationData":[OSD([subQ1,subQ0,sQuery(id+"F18.wireOp",EDGE,"E10.bottom"),sQuery(id+"F18.wireOp",EDGE,"E10.top"),sQuery(id+"F18.wireOp",EDGE,"E10.left"),sQuery(id+"F18.wireOp",EDGE,"E10.right")])],"isStart":false})]}),makeQuery(id+"F21.opExtrude","CAP_FACE",FACE,{"disambiguationData":[OSD([sQuery(id+"F20.wireOp",EDGE,"E11.bottom"),sQuery(id+"F20.wireOp",EDGE,"E11.top"),sQuery(id+"F20.wireOp",EDGE,"E11.left"),sQuery(id+"F20.wireOp",EDGE,"E11.right")])],"isStart":false})]}),makeQuery(id+"F23.opExtrude","CAP_FACE",FACE,{"disambiguationData":[OSD([sQuery(id+"F22.wireOp",EDGE,"E12.bottom"),sQuery(id+"F22.wireOp",EDGE,"E12.top"),sQuery(id+"F22.wireOp",EDGE,"E12.left"),sQuery(id+"F22.wireOp",EDGE,"E12.right")])],"isStart":false})]}),makeQuery(id+"F25.opExtrude","CAP_FACE",FACE,{"disambiguationData":[OSD([sQuery(id+"F24.wireOp",EDGE,"E13.bottom"),sQuery(id+"F24.wireOp",EDGE,"E13.top"),sQuery(id+"F24.wireOp",EDGE,"E13.left"),sQuery(id+"F24.wireOp",EDGE,"E13.right")])],"isStart":false})]}),makeQuery(id+"F27.opExtrude","CAP_FACE",FACE,{"disambiguationData":[OSD([sQuery(id+"F26.wireOp",EDGE,"E14.bottom"),sQuery(id+"F26.wireOp",EDGE,"E14.top"),sQuery(id+"F26.wireOp",EDGE,"E14.left"),sQuery(id+"F26.wireOp",EDGE,"E14.right")])],"isStart":false})]}),makeQuery(id+"F29.opExtrude","CAP_FACE",FACE,{"disambiguationData":[OSD([sQuery(id+"F28.wireOp",EDGE,"E15.bottom"),sQuery(id+"F28.wireOp",EDGE,"E15.top"),sQuery(id+"F28.wireOp",EDGE,"E15.left"),sQuery(id+"F28.wireOp",EDGE,"E15.right")])],"isStart":false})]}),makeQuery(id+"F31.opExtrude","CAP_FACE",FACE,{"disambiguationData":[OSD([sQuery(id+"F30.wireOp",EDGE,"E16.bottom"),sQuery(id+"F30.wireOp",EDGE,"E16.top"),sQuery(id+"F30.wireOp",EDGE,"E16.left"),sQuery(id+"F30.wireOp",EDGE,"E16.right")])],"isStart":false})]}),makeQuery(id+"F33.opExtrude","CAP_FACE",FACE,{"disambiguationData":[OSD([sQuery(id+"F32.wireOp",EDGE,"E17.bottom"),sQuery(id+"F32.wireOp",EDGE,"E17.top"),sQuery(id+"F32.wireOp",EDGE,"E17.left"),sQuery(id+"F32.wireOp",EDGE,"E17.right")])],"isStart":false})]}),makeQuery(id+"F35.opExtrude","CAP_FACE",FACE,{"disambiguationData":[OSD([sQuery(id+"F34.wireOp",EDGE,"E18.bottom"),sQuery(id+"F34.wireOp",EDGE,"E18.top"),sQuery(id+"F34.wireOp",EDGE,"E18.left"),sQuery(id+"F34.wireOp",EDGE,"E18.right"),sQuery(id+"F34.wireOp",EDGE,"E19.top"),sQuery(id+"F34.wireOp",EDGE,"E19.left"),sQuery(id+"F34.wireOp",EDGE,"E19.right")])],"isStart":false})]}),makeQuery(id+"F37.opExtrude","CAP_FACE",FACE,{"disambiguationData":[OSD([sQuery(id+"F36.wireOp",EDGE,"E20.bottom"),sQuery(id+"F36.wireOp",EDGE,"E20.top"),sQuery(id+"F36.wireOp",EDGE,"E20.left"),sQuery(id+"F36.wireOp",EDGE,"E20.right")])],"isStart":false})]}),makeQuery(id+"F39.opExtrude","CAP_FACE",FACE,{"disambiguationData":[OSD([sQuery(id+"F38.wireOp",EDGE,"E21.bottom"),sQuery(id+"F38.wireOp",EDGE,"E21.top"),sQuery(id+"F38.wireOp",EDGE,"E21.left"),sQuery(id+"F38.wireOp",EDGE,"E21.right")])],"isStart":false})]}),makeQuery(id+"F41.opExtrude","CAP_FACE",FACE,{"disambiguationData":[OSD([sQuery(id+"F40.wireOp",EDGE,"E22.bottom"),sQuery(id+"F40.wireOp",EDGE,"E22.top"),sQuery(id+"F40.wireOp",EDGE,"E22.left"),sQuery(id+"F40.wireOp",EDGE,"E22.right")])],"isStart":false})]}),makeQuery(id+"F43.opExtrude","CAP_FACE",FACE,{"disambiguationData":[OSD([sQuery(id+"F42.wireOp",EDGE,"E23.bottom"),sQuery(id+"F42.wireOp",EDGE,"E23.top"),sQuery(id+"F42.wireOp",EDGE,"E23.left"),sQuery(id+"F42.wireOp",EDGE,"E23.right")])],"isStart":false})]}),makeQuery(id+"F45.opExtrude","CAP_FACE",FACE,{"disambiguationData":[OSD([sQuery(id+"F44.wireOp",EDGE,"E24.bottom"),sQuery(id+"F44.wireOp",EDGE,"E24.top"),sQuery(id+"F44.wireOp",EDGE,"E24.left"),sQuery(id+"F44.wireOp",EDGE,"E24.right")])],"isStart":false})]}),makeQuery(id+"F47.opExtrude","CAP_FACE",FACE,{"disambiguationData":[OSD([sQuery(id+"F46.wireOp",EDGE,"E25.bottom"),sQuery(id+"F46.wireOp",EDGE,"E25.top"),sQuery(id+"F46.wireOp",EDGE,"E25.left"),sQuery(id+"F46.wireOp",EDGE,"E25.right")])],"isStart":false})]}),makeQuery(id+"F49.opExtrude","CAP_FACE",FACE,{"disambiguationData":[OSD([sQuery(id+"F48.wireOp",EDGE,"E26"),sQuery(id+"F48.wireOp",EDGE,"E27"),sQuery(id+"F48.wireOp",EDGE,"E28"),sQuery(id+"F48.wireOp",EDGE,"E29"),sQuery(id+"F48.wireOp",EDGE,"E30"),sQuery(id+"F48.wireOp",EDGE,"E31"),sQuery(id+"F48.wireOp",EDGE,"E36"),sQuery(id+"F48.wireOp",EDGE,"E37"),sQuery(id+"F48.wireOp",EDGE,"E38"),sQuery(id+"F48.wireOp",EDGE,"E39"),sQuery(id+"F48.wireOp",EDGE,"E40"),sQuery(id+"F48.wireOp",EDGE,"E41")])],"isStart":false}),makeQuery(id+"F49.opExtrude","CAP_FACE",FACE,{"disambiguationData":[OSD([sQuery(id+"F48.wireOp",EDGE,"E32"),sQuery(id+"F48.wireOp",EDGE,"E33"),sQuery(id+"F48.wireOp",EDGE,"E34"),sQuery(id+"F48.wireOp",EDGE,"E35")])],"isStart":false})]}),makeQuery(id+"F51.opExtrude","CAP_FACE",FACE,{"disambiguationData":[OSD([sQuery(id+"F50.wireOp",EDGE,"E42"),sQuery(id+"F50.wireOp",EDGE,"E43"),sQuery(id+"F50.wireOp",EDGE,"E44"),sQuery(id+"F50.wireOp",EDGE,"E45"),sQuery(id+"F50.wireOp",EDGE,"E46"),sQuery(id+"F50.wireOp",EDGE,"E47"),sQuery(id+"F50.wireOp",EDGE,"E48"),sQuery(id+"F50.wireOp",EDGE,"E49"),sQuery(id+"F50.wireOp",EDGE,"E50"),sQuery(id+"F50.wireOp",EDGE,"E51"),sQuery(id+"F50.wireOp",EDGE,"E52"),sQuery(id+"F50.wireOp",EDGE,"E53"),sQuery(id+"F50.wireOp",EDGE,"E55.left"),sQuery(id+"F50.wireOp",EDGE,"E55.right")])],"isStart":false})]});}
            var sketch = newSketch(context, id + "F52", { "sketchPlane" : qUnion([Q0])});
            skLineSegment(sketch, "E56.bottom", {"start": v(29.74, 60.72) * mm, "end": v(30.33, 60.72) * mm});
            skLineSegment(sketch, "E56.top", {"start": v(29.74, 59.1) * mm, "end": v(30.33, 59.1) * mm});
            skLineSegment(sketch, "E56.left", {"start": v(29.74, 60.72) * mm, "end": v(29.74, 59.1) * mm});
            skLineSegment(sketch, "E56.right", {"start": v(30.33, 60.72) * mm, "end": v(30.33, 59.1) * mm});
            skSolve(sketch);
        }
        {
            var Q0;
            Q0=makeQuery(id+"F52.imprint","IMPRINT",FACE,{"disambiguationData":[TD([[makeQuery(id+"F52.imprint","IMPRINT",EDGE,{"derivedFrom":sQuery(id+"F52.wireOp",EDGE,"E56.bottom")}),-1.0]])]});
            extrude(context, id + "F53", {"entities" : qUnion([Q0]), "operationType" : NewBodyOperationType.REMOVE, "oppositeDirection" : true, "depth" : 12.7 * mm, "offsetDistance" : 25.4 * mm});
        }
        {
            var Q0;
            {var subQ3=sQuery(id+"F2.wireOp",EDGE,"E1.bottom");var subQ4=makeQuery(id+"F3.boolean.opBoolean","COPY",FACE,{"derivedFrom":makeQuery(id+"F3.opExtrude","SWEPT_FACE",FACE,{"disambiguationData":[OSD([subQ3])]})});var subQ6=sQuery(id+"F2.wireOp",EDGE,"E1.left");var subQ7=makeQuery(id+"F3.boolean.opBoolean","COPY",FACE,{"derivedFrom":makeQuery(id+"F3.opExtrude","SWEPT_FACE",FACE,{"disambiguationData":[OSD([subQ6])]})});var subQ11=sQuery(id+"F2.wireOp",EDGE,"E1.right");var subQ18=sQuery(id+"F2.wireOp",EDGE,"E1.top");Q0=makeQuery(id+"F51.boolean.opBoolean","SPLIT",FACE,{"disambiguationData":[TD([subQ7])],"derivedFrom":makeQuery(id+"F49.boolean.opBoolean","SPLIT",FACE,{"disambiguationData":[TD([subQ4])],"derivedFrom":makeQuery(id+"F41.boolean.opBoolean","SPLIT",FACE,{"disambiguationData":[TD([subQ4])],"derivedFrom":makeQuery(id+"F33.boolean.opBoolean","SPLIT",FACE,{"disambiguationData":[TD([subQ4])],"derivedFrom":makeQuery(id+"F13.boolean.opBoolean","SPLIT",FACE,{"disambiguationData":[TD([subQ4])],"derivedFrom":makeQuery(id+"F9.boolean.opBoolean","SPLIT",FACE,{"disambiguationData":[TD([subQ4])],"derivedFrom":makeQuery(id+"F3.boolean.opBoolean","COPY",FACE,{"derivedFrom":makeQuery(id+"F3.opExtrude","CAP_FACE",FACE,{"disambiguationData":[OSD([subQ3,subQ18,subQ6,subQ11])],"isStart":false})})})})})})})});}
            var sketch = newSketch(context, id + "F54", { "sketchPlane" : qUnion([Q0])});
            skLineSegment(sketch, "E57", {"start": v(38.88, 61.24) * mm, "end": v(39.09, 61.24) * mm});
            skLineSegment(sketch, "E58", {"start": v(39.09, 61.24) * mm, "end": v(39.09, 47) * mm});
            skLineSegment(sketch, "E59", {"start": v(39.09, 47) * mm, "end": v(48.4, 47) * mm});
            skLineSegment(sketch, "E60", {"start": v(48.4, 47) * mm, "end": v(48.4, 48.33) * mm});
            skLineSegment(sketch, "E61", {"start": v(48.4, 48.33) * mm, "end": v(48.02, 48.33) * mm});
            skLineSegment(sketch, "E62", {"start": v(48.02, 48.33) * mm, "end": v(48, 55.9) * mm});
            skLineSegment(sketch, "E63", {"start": v(48, 55.9) * mm, "end": v(48.38, 55.9) * mm});
            skLineSegment(sketch, "E64", {"start": v(48.38, 55.9) * mm, "end": v(48.38, 58.46) * mm});
            skLineSegment(sketch, "E65", {"start": v(48.38, 58.46) * mm, "end": v(48, 58.46) * mm});
            skLineSegment(sketch, "E66", {"start": v(48, 58.46) * mm, "end": v(48.02, 66.04) * mm});
            skLineSegment(sketch, "E67", {"start": v(48.02, 66.04) * mm, "end": v(48.4, 66.04) * mm});
            skLineSegment(sketch, "E68", {"start": v(48.4, 66.04) * mm, "end": v(48.4, 67.37) * mm});
            skLineSegment(sketch, "E69", {"start": v(48.4, 67.37) * mm, "end": v(39.09, 67.35) * mm});
            skLineSegment(sketch, "E70", {"start": v(39.09, 67.35) * mm, "end": v(39.1, 63.32) * mm});
            skLineSegment(sketch, "E71", {"start": v(39.1, 63.32) * mm, "end": v(38.87, 63.32) * mm});
            skLineSegment(sketch, "E72", {"start": v(38.87, 63.32) * mm, "end": v(38.88, 61.24) * mm});
            skLineSegment(sketch, "E73", {"start": v(36.72, 61.24) * mm, "end": v(36.72, 44.6) * mm});
            skLineSegment(sketch, "E74", {"start": v(36.72, 44.6) * mm, "end": v(68.45, 44.67) * mm});
            skLineSegment(sketch, "E75", {"start": v(68.45, 44.67) * mm, "end": v(68.45, 67.44) * mm});
            skLineSegment(sketch, "E76", {"start": v(68.45, 67.44) * mm, "end": v(36.72, 67.44) * mm});
            skLineSegment(sketch, "E77", {"start": v(36.72, 67.44) * mm, "end": v(36.72, 44.6) * mm});
            skSolve(sketch);
        }
        {
            var Q0;
            Q0=makeQuery(id+"F54.imprint","IMPRINT",FACE,{"disambiguationData":[TD([[makeQuery(id+"F54.imprint","IMPRINT",EDGE,{"derivedFrom":sQuery(id+"F54.wireOp",EDGE,"E57")}),-1.0]])]});
            extrude(context, id + "F55", {"entities" : qUnion([Q0]), "operationType" : NewBodyOperationType.ADD, "depth" : 12.7 * mm, "offsetDistance" : 25.4 * mm});
        }
        {
            var Q0;
            {var subQ4=sQuery(id+"F2.wireOp",EDGE,"E1.bottom");var subQ5=makeQuery(id+"F3.boolean.opBoolean","COPY",FACE,{"derivedFrom":makeQuery(id+"F3.opExtrude","SWEPT_FACE",FACE,{"disambiguationData":[OSD([subQ4])]})});var subQ7=sQuery(id+"F2.wireOp",EDGE,"E1.left");var subQ8=makeQuery(id+"F3.boolean.opBoolean","COPY",FACE,{"derivedFrom":makeQuery(id+"F3.opExtrude","SWEPT_FACE",FACE,{"disambiguationData":[OSD([subQ7])]})});var subQ13=sQuery(id+"F2.wireOp",EDGE,"E1.right");var subQ20=sQuery(id+"F2.wireOp",EDGE,"E1.top");Q0=makeQuery(id+"F55.boolean.opBoolean","SPLIT",FACE,{"disambiguationData":[TD([subQ5])],"derivedFrom":makeQuery(id+"F51.boolean.opBoolean","SPLIT",FACE,{"disambiguationData":[TD([subQ8])],"derivedFrom":makeQuery(id+"F49.boolean.opBoolean","SPLIT",FACE,{"disambiguationData":[TD([subQ5])],"derivedFrom":makeQuery(id+"F41.boolean.opBoolean","SPLIT",FACE,{"disambiguationData":[TD([subQ5])],"derivedFrom":makeQuery(id+"F33.boolean.opBoolean","SPLIT",FACE,{"disambiguationData":[TD([subQ5])],"derivedFrom":makeQuery(id+"F13.boolean.opBoolean","SPLIT",FACE,{"disambiguationData":[TD([subQ5])],"derivedFrom":makeQuery(id+"F9.boolean.opBoolean","SPLIT",FACE,{"disambiguationData":[TD([subQ5])],"derivedFrom":makeQuery(id+"F3.boolean.opBoolean","COPY",FACE,{"derivedFrom":makeQuery(id+"F3.opExtrude","CAP_FACE",FACE,{"disambiguationData":[OSD([subQ4,subQ20,subQ7,subQ13])],"isStart":false})})})})})})})})});}
            var sketch = newSketch(context, id + "F56", { "sketchPlane" : qUnion([Q0])});
            skLineSegment(sketch, "E78.bottom", {"start": v(36.72, 44.6) * mm, "end": v(-56.12, 44.6) * mm});
            skLineSegment(sketch, "E78.top", {"start": v(36.72, 47.59) * mm, "end": v(-56.12, 47.59) * mm});
            skLineSegment(sketch, "E78.left", {"start": v(36.72, 44.6) * mm, "end": v(36.72, 47.59) * mm});
            skLineSegment(sketch, "E78.right", {"start": v(-56.12, 44.6) * mm, "end": v(-56.12, 47.59) * mm});
            skSolve(sketch);
        }
        {
            var Q0;
            Q0=makeQuery(id+"F56.imprint","IMPRINT",FACE,{"disambiguationData":[TD([[makeQuery(id+"F56.imprint","IMPRINT",EDGE,{"derivedFrom":sQuery(id+"F56.wireOp",EDGE,"E78.bottom")}),-1.0]])]});
            extrude(context, id + "F57", {"entities" : qUnion([Q0]), "operationType" : NewBodyOperationType.ADD, "depth" : 12.7 * mm, "offsetDistance" : 25.4 * mm});
        }
        {
            var Q0;
            {var subQ3=sQuery(id+"F2.wireOp",EDGE,"E1.left");var subQ4=makeQuery(id+"F3.boolean.opBoolean","COPY",FACE,{"derivedFrom":makeQuery(id+"F3.opExtrude","SWEPT_FACE",FACE,{"disambiguationData":[OSD([subQ3])]})});var subQ10=sQuery(id+"F2.wireOp",EDGE,"E1.bottom");var subQ11=makeQuery(id+"F3.boolean.opBoolean","COPY",FACE,{"derivedFrom":makeQuery(id+"F3.opExtrude","SWEPT_FACE",FACE,{"disambiguationData":[OSD([subQ10])]})});var subQ14=sQuery(id+"F2.wireOp",EDGE,"E1.right");var subQ21=sQuery(id+"F2.wireOp",EDGE,"E1.top");Q0=makeQuery(id+"F57.boolean.opBoolean","SPLIT",FACE,{"disambiguationData":[TD([subQ4])],"derivedFrom":makeQuery(id+"F55.boolean.opBoolean","SPLIT",FACE,{"disambiguationData":[TD([subQ11])],"derivedFrom":makeQuery(id+"F51.boolean.opBoolean","SPLIT",FACE,{"disambiguationData":[TD([subQ4])],"derivedFrom":makeQuery(id+"F49.boolean.opBoolean","SPLIT",FACE,{"disambiguationData":[TD([subQ11])],"derivedFrom":makeQuery(id+"F41.boolean.opBoolean","SPLIT",FACE,{"disambiguationData":[TD([subQ11])],"derivedFrom":makeQuery(id+"F33.boolean.opBoolean","SPLIT",FACE,{"disambiguationData":[TD([subQ11])],"derivedFrom":makeQuery(id+"F13.boolean.opBoolean","SPLIT",FACE,{"disambiguationData":[TD([subQ11])],"derivedFrom":makeQuery(id+"F9.boolean.opBoolean","SPLIT",FACE,{"disambiguationData":[TD([subQ11])],"derivedFrom":makeQuery(id+"F3.boolean.opBoolean","COPY",FACE,{"derivedFrom":makeQuery(id+"F3.opExtrude","CAP_FACE",FACE,{"disambiguationData":[OSD([subQ10,subQ21,subQ3,subQ14])],"isStart":false})})})})})})})})})});}
            extrude(context, id + "F58", {"entities" : qUnion([Q0]), "operationType" : NewBodyOperationType.ADD, "depth" : 12.7 * mm, "offsetDistance" : 25.4 * mm});
        }
        {
            var Q0;
            {var subQ0=sQuery(id+"F2.wireOp",EDGE,"E1.bottom");var subQ1=makeQuery(id+"F3.boolean.opBoolean","COPY",FACE,{"derivedFrom":makeQuery(id+"F3.opExtrude","SWEPT_FACE",FACE,{"disambiguationData":[OSD([subQ0])]})});var subQ8=sQuery(id+"F2.wireOp",EDGE,"E1.left");var subQ9=makeQuery(id+"F3.boolean.opBoolean","COPY",FACE,{"derivedFrom":makeQuery(id+"F3.opExtrude","SWEPT_FACE",FACE,{"disambiguationData":[OSD([subQ8])]})});var subQ13=sQuery(id+"F2.wireOp",EDGE,"E1.right");var subQ20=sQuery(id+"F2.wireOp",EDGE,"E1.top");Q0=makeQuery(id+"F57.boolean.opBoolean","SPLIT",FACE,{"disambiguationData":[TD([subQ1])],"derivedFrom":makeQuery(id+"F55.boolean.opBoolean","SPLIT",FACE,{"disambiguationData":[TD([subQ1])],"derivedFrom":makeQuery(id+"F51.boolean.opBoolean","SPLIT",FACE,{"disambiguationData":[TD([subQ9])],"derivedFrom":makeQuery(id+"F49.boolean.opBoolean","SPLIT",FACE,{"disambiguationData":[TD([subQ1])],"derivedFrom":makeQuery(id+"F41.boolean.opBoolean","SPLIT",FACE,{"disambiguationData":[TD([subQ1])],"derivedFrom":makeQuery(id+"F33.boolean.opBoolean","SPLIT",FACE,{"disambiguationData":[TD([subQ1])],"derivedFrom":makeQuery(id+"F13.boolean.opBoolean","SPLIT",FACE,{"disambiguationData":[TD([subQ1])],"derivedFrom":makeQuery(id+"F9.boolean.opBoolean","SPLIT",FACE,{"disambiguationData":[TD([subQ1])],"derivedFrom":makeQuery(id+"F3.boolean.opBoolean","COPY",FACE,{"derivedFrom":makeQuery(id+"F3.opExtrude","CAP_FACE",FACE,{"disambiguationData":[OSD([subQ0,subQ20,subQ8,subQ13])],"isStart":false})})})})})})})})})});}
            var sketch = newSketch(context, id + "F59", { "sketchPlane" : qUnion([Q0])});
            skLineSegment(sketch, "E79", {"start": v(-5.91, 54.96) * mm, "end": v(-5.91, 52.94) * mm});
            skLineSegment(sketch, "E80", {"start": v(-5.91, 52.94) * mm, "end": v(-5.1, 52.94) * mm});
            skLineSegment(sketch, "E81", {"start": v(-5.1, 52.94) * mm, "end": v(-5.1, 52.38) * mm});
            skLineSegment(sketch, "E82", {"start": v(-4.19, 51.98) * mm, "end": v(-5.1, 51.98) * mm});
            skLineSegment(sketch, "E83", {"start": v(-5.1, 51.98) * mm, "end": v(-5.1, 52.38) * mm});
            skLineSegment(sketch, "E84", {"start": v(-4.19, 51.98) * mm, "end": v(-4.19, 51.32) * mm});
            skLineSegment(sketch, "E85", {"start": v(-4.19, 51.32) * mm, "end": v(7.12, 51.32) * mm});
            skLineSegment(sketch, "E86", {"start": v(7.12, 51.32) * mm, "end": v(7.12, 51.98) * mm});
            skLineSegment(sketch, "E87", {"start": v(7.12, 51.98) * mm, "end": v(8.02, 51.98) * mm});
            skLineSegment(sketch, "E88", {"start": v(8.02, 51.98) * mm, "end": v(8.02, 52.94) * mm});
            skLineSegment(sketch, "E89", {"start": v(8.02, 52.94) * mm, "end": v(8.84, 52.94) * mm});
            skLineSegment(sketch, "E90", {"start": v(8.84, 52.94) * mm, "end": v(8.84, 54.96) * mm});
            skLineSegment(sketch, "E91", {"start": v(8.84, 54.96) * mm, "end": v(8.98, 54.98) * mm});
            skLineSegment(sketch, "E92", {"start": v(8.98, 54.98) * mm, "end": v(9.14, 55) * mm});
            skLineSegment(sketch, "E93", {"start": v(9.14, 55) * mm, "end": v(9.2, 55) * mm});
            skLineSegment(sketch, "E94", {"start": v(9.2, 55) * mm, "end": v(9.23, 55.02) * mm});
            skLineSegment(sketch, "E95", {"start": v(9.23, 55.02) * mm, "end": v(9.27, 55.04) * mm});
            skLineSegment(sketch, "E96", {"start": v(9.27, 55.04) * mm, "end": v(9.27, 55.06) * mm});
            skLineSegment(sketch, "E97", {"start": v(9.27, 55.06) * mm, "end": v(9.27, 56.46) * mm});
            skLineSegment(sketch, "E98", {"start": v(9.27, 56.46) * mm, "end": v(9.27, 56.47) * mm});
            skLineSegment(sketch, "E99", {"start": v(9.27, 56.47) * mm, "end": v(9.23, 56.5) * mm});
            skLineSegment(sketch, "E100", {"start": v(9.23, 56.5) * mm, "end": v(9.14, 56.52) * mm});
            skLineSegment(sketch, "E101", {"start": v(9.14, 56.52) * mm, "end": v(8.84, 56.55) * mm});
            skLineSegment(sketch, "E102", {"start": v(8.84, 56.55) * mm, "end": v(8.84, 61.76) * mm});
            skLineSegment(sketch, "E103", {"start": v(8.84, 61.76) * mm, "end": v(9.23, 61.8) * mm});
            skLineSegment(sketch, "E104", {"start": v(9.23, 61.8) * mm, "end": v(9.27, 61.84) * mm});
            skLineSegment(sketch, "E105", {"start": v(9.27, 61.84) * mm, "end": v(9.27, 63.27) * mm});
            skLineSegment(sketch, "E106", {"start": v(9.27, 63.27) * mm, "end": v(9.23, 63.3) * mm});
            skLineSegment(sketch, "E107", {"start": v(9.23, 63.3) * mm, "end": v(8.84, 63.35) * mm});
            skLineSegment(sketch, "E108", {"start": v(8.84, 63.35) * mm, "end": v(8.84, 65.38) * mm});
            skLineSegment(sketch, "E109", {"start": v(8.84, 65.38) * mm, "end": v(8.02, 65.38) * mm});
            skLineSegment(sketch, "E110", {"start": v(8.02, 65.38) * mm, "end": v(8.02, 66.34) * mm});
            skLineSegment(sketch, "E111", {"start": v(8.02, 66.34) * mm, "end": v(7.13, 66.34) * mm});
            skLineSegment(sketch, "E112", {"start": v(7.13, 66.34) * mm, "end": v(7.13, 67) * mm});
            skLineSegment(sketch, "E113", {"start": v(7.13, 67) * mm, "end": v(-4.19, 67) * mm});
            skLineSegment(sketch, "E114", {"start": v(-4.19, 67) * mm, "end": v(-4.19, 66.36) * mm});
            skLineSegment(sketch, "E115", {"start": v(-4.19, 66.36) * mm, "end": v(-5.1, 66.36) * mm});
            skLineSegment(sketch, "E116", {"start": v(-5.1, 66.36) * mm, "end": v(-5.1, 65.4) * mm});
            skLineSegment(sketch, "E117", {"start": v(-5.1, 65.4) * mm, "end": v(-5.93, 65.4) * mm});
            skLineSegment(sketch, "E118", {"start": v(-5.93, 65.4) * mm, "end": v(-5.93, 63.35) * mm});
            skLineSegment(sketch, "E119", {"start": v(-5.93, 63.35) * mm, "end": v(-6.35, 63.3) * mm});
            skLineSegment(sketch, "E120", {"start": v(-6.35, 63.3) * mm, "end": v(-6.35, 61.8) * mm});
            skLineSegment(sketch, "E121", {"start": v(-6.35, 61.8) * mm, "end": v(-5.93, 61.76) * mm});
            skLineSegment(sketch, "E122", {"start": v(-5.93, 61.76) * mm, "end": v(-5.93, 56.56) * mm});
            skLineSegment(sketch, "E123", {"start": v(-5.93, 56.56) * mm, "end": v(-6.4, 56.5) * mm});
            skLineSegment(sketch, "E124", {"start": v(-6.35, 56.57) * mm, "end": v(-6.35, 55) * mm});
            skLineSegment(sketch, "E125", {"start": v(-6.35, 55) * mm, "end": v(-5.91, 54.96) * mm});
            skLineSegment(sketch, "E126", {"start": v(-7.62, 47.59) * mm, "end": v(11, 47.59) * mm});
            skLineSegment(sketch, "E127", {"start": v(11, 47.59) * mm, "end": v(11, 67.44) * mm});
            skLineSegment(sketch, "E128", {"start": v(11, 67.44) * mm, "end": v(-7.62, 67.44) * mm});
            skLineSegment(sketch, "E129", {"start": v(-7.62, 67.44) * mm, "end": v(-7.62, 47.59) * mm});
            skSolve(sketch);
        }
        {
            var Q0;
            Q0=makeQuery(id+"F59.imprint","IMPRINT",FACE,{"disambiguationData":[TD([[makeQuery(id+"F59.imprint","IMPRINT",EDGE,{"derivedFrom":sQuery(id+"F59.wireOp",EDGE,"E79")}),-1.0]])]});
            extrude(context, id + "F60", {"entities" : qUnion([Q0]), "operationType" : NewBodyOperationType.ADD, "depth" : 12.7 * mm, "offsetDistance" : 25.4 * mm});
        }
        {
            var Q0;
            {var subQ2=sQuery(id+"F2.wireOp",EDGE,"E1.top");var subQ3=makeQuery(id+"F3.boolean.opBoolean","COPY",FACE,{"derivedFrom":makeQuery(id+"F3.opExtrude","SWEPT_FACE",FACE,{"disambiguationData":[OSD([subQ2])]})});var subQ4=sQuery(id+"F2.wireOp",EDGE,"E1.right");var subQ5=sQuery(id+"F2.wireOp",EDGE,"E1.left");var subQ6=sQuery(id+"F2.wireOp",EDGE,"E1.bottom");Q0=makeQuery(id+"F13.boolean.opBoolean","SPLIT",FACE,{"disambiguationData":[TD([subQ3])],"derivedFrom":makeQuery(id+"F9.boolean.opBoolean","SPLIT",FACE,{"disambiguationData":[TD([makeQuery(id+"F3.boolean.opBoolean","COPY",FACE,{"derivedFrom":makeQuery(id+"F3.opExtrude","SWEPT_FACE",FACE,{"disambiguationData":[OSD([subQ6])]})})])],"derivedFrom":makeQuery(id+"F3.boolean.opBoolean","COPY",FACE,{"derivedFrom":makeQuery(id+"F3.opExtrude","CAP_FACE",FACE,{"disambiguationData":[OSD([subQ6,subQ2,subQ5,subQ4])],"isStart":false})})})});}
            var sketch = newSketch(context, id + "F61", { "sketchPlane" : qUnion([Q0])});
            skLineSegment(sketch, "E130.bottom", {"start": v(-1.27, -59.82) * mm, "end": v(1.27, -59.82) * mm});
            skLineSegment(sketch, "E130.top", {"start": v(-1.27, -67.44) * mm, "end": v(1.27, -67.44) * mm});
            skLineSegment(sketch, "E130.left", {"start": v(-1.27, -59.82) * mm, "end": v(-1.27, -67.44) * mm});
            skLineSegment(sketch, "E130.right", {"start": v(1.27, -59.82) * mm, "end": v(1.27, -67.44) * mm});
            skSolve(sketch);
        }
        {
            var Q0;
            Q0=makeQuery(id+"F61.imprint","IMPRINT",FACE,{"disambiguationData":[TD([[makeQuery(id+"F61.imprint","IMPRINT",EDGE,{"derivedFrom":sQuery(id+"F61.wireOp",EDGE,"E130.bottom")}),1.0]])]});
            extrude(context, id + "F62", {"entities" : qUnion([Q0]), "operationType" : NewBodyOperationType.ADD, "depth" : 12.7 * mm, "offsetDistance" : 25.4 * mm});
        }
    });
